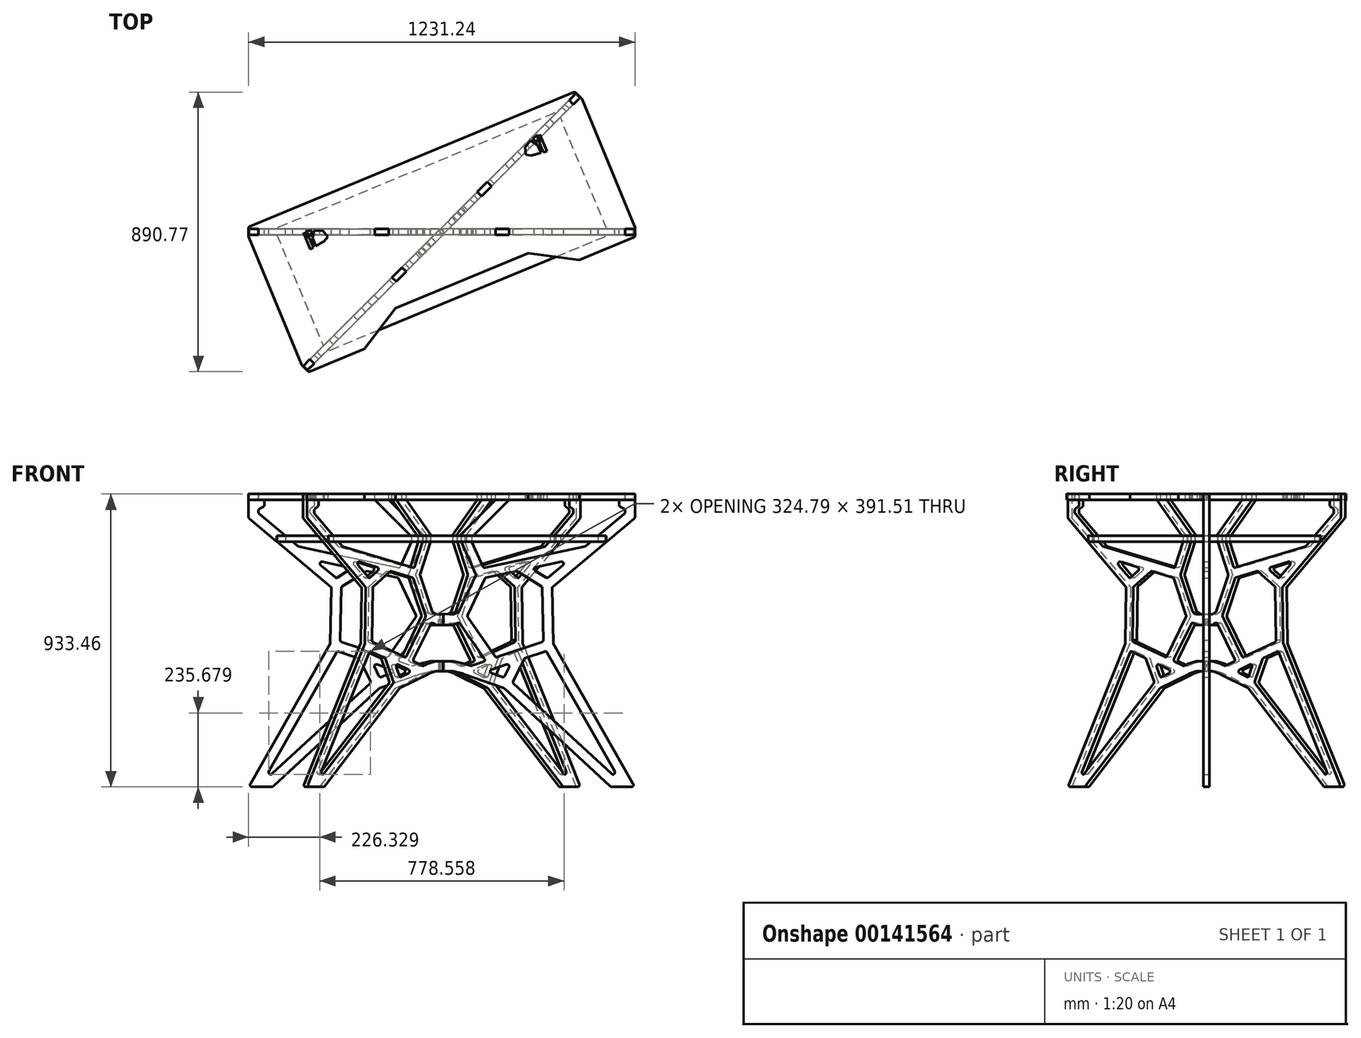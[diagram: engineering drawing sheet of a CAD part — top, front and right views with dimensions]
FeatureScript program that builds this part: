
annotation { "Feature Type Name" : "Feature", "Feature Type Description" : "" }
export const myFeature = defineFeature(function(context is Context, id is Id, definition is map)
    precondition{}
    {
        {
            var Q0;
            Q0=qCreatedBy(makeId("Front.planeOp"),FACE);
            var sketch = newSketch(context, id + "F0", { "sketchPlane" : qUnion([Q0])});
            skLineSegment(sketch, "E0.bottom", {"start": v(-726.46, -550.82) * mm, "end": v(-663.66, -550.82) * mm});
            skLineSegment(sketch, "E0.top", {"start": v(-737.38, 382.63) * mm, "end": v(-705.63, 382.63) * mm});
            skLineSegment(sketch, "E0.left", {"start": v(-737.38, -93.62) * mm, "end": v(-737.38, 230.23) * mm});
            skLineSegment(sketch, "E1", {"start": v(-705.63, 363.58) * mm, "end": v(-686.58, 363.58) * mm});
            skLineSegment(sketch, "E2.bottom", {"start": v(-737.38, 230.23) * mm, "end": v(493.44, 230.23) * mm, "construction": true});
            skLineSegment(sketch, "E2.top", {"start": v(-737.38, 211.18) * mm, "end": v(493.44, 211.18) * mm, "construction": true});
            skLineSegment(sketch, "E2.left", {"start": v(-737.38, 230.23) * mm, "end": v(-737.38, 211.18) * mm});
            skLineSegment(sketch, "E2.right", {"start": v(493.44, 230.23) * mm, "end": v(493.44, 211.18) * mm});
            skLineSegment(sketch, "E3", {"start": v(-735.1, 304.53) * mm, "end": v(-475.84, 87.44) * mm});
            skLineSegment(sketch, "E4", {"start": v(-473.57, 82.44) * mm, "end": v(-477.15, -92) * mm});
            skLineSegment(sketch, "E5", {"start": v(-477.98, -95.02) * mm, "end": v(-731.98, -541.32) * mm});
            skLineSegment(sketch, "E6", {"start": v(-737.38, -93.62) * mm, "end": v(493.78, -93.62) * mm, "construction": true});
            skLineSegment(sketch, "E7", {"start": v(-726.46, -550.82) * mm, "end": v(-661.18, -550.82) * mm});
            skLineSegment(sketch, "E8", {"start": v(-659.36, -549.13) * mm, "end": v(-321.3, -237.33) * mm});
            skLineSegment(sketch, "E9", {"start": v(-319.11, -236) * mm, "end": v(-190.82, -190.7) * mm});
            skLineSegment(sketch, "E10", {"start": v(-190.2, -190.52) * mm, "end": v(-123.3, -174.31) * mm});
            skLineSegment(sketch, "E11", {"start": v(-182.24, 230.23) * mm, "end": v(-228.58, 128.01) * mm});
            skLineSegment(sketch, "E12", {"start": v(-228.55, 122.7) * mm, "end": v(-175.03, 8.55) * mm});
            skLineSegment(sketch, "E13", {"start": v(-171.72, 5.38) * mm, "end": v(-124.24, -14.36) * mm});
            skLineSegment(sketch, "E14", {"start": v(-553, 193.46) * mm, "end": v(-261.6, 132.05) * mm, "construction": true});
            skLineSegment(sketch, "E15", {"start": v(-473.5, 85.48) * mm, "end": v(-383.92, 141.6) * mm, "construction": true});
            skLineSegment(sketch, "E16", {"start": v(-477.18, -93.62) * mm, "end": v(-239.21, -174.12) * mm, "construction": true});
            skLineSegment(sketch, "E17", {"start": v(-320.34, -236.44) * mm, "end": v(-364, -148.67) * mm, "construction": true});
            skLineSegment(sketch, "E18", {"start": v(-192.54, -20.35) * mm, "end": v(-278.62, -144.03) * mm, "construction": true});
            skLineSegment(sketch, "E19.0", {"start": v(-662.9, -509.21) * mm, "end": v(-350.73, -221.27) * mm});
            skLineSegment(sketch, "E20.0", {"start": v(-457.14, -122.59) * mm, "end": v(-672.73, -501.4) * mm});
            skLineSegment(sketch, "E21.0", {"start": v(-199.25, -160.05) * mm, "end": v(-123.3, -141.64) * mm});
            skLineSegment(sketch, "E21.1", {"start": v(-314.2, -200.6) * mm, "end": v(-280.77, -188.8) * mm});
            skLineSegment(sketch, "E22.0", {"start": v(-172.82, -28.55) * mm, "end": v(-124.24, -48.75) * mm});
            skLineSegment(sketch, "E22.1", {"start": v(-258.92, 112.68) * mm, "end": v(-204.28, -3.86) * mm});
            skLineSegment(sketch, "E23.0", {"start": v(-705.63, 324.22) * mm, "end": v(-705.63, 329.87) * mm});
            skLineSegment(sketch, "E24.0", {"start": v(-703.36, 319.36) * mm, "end": v(-580.12, 216.16) * mm});
            skLineSegment(sketch, "E25.0", {"start": v(-441.8, 83.23) * mm, "end": v(-445.22, -83.58) * mm});
            skLineSegment(sketch, "E26.0", {"start": v(-502.23, 166.54) * mm, "end": v(-421.69, 149.57) * mm});
            skLineSegment(sketch, "E27.0", {"start": v(-577.35, 214.82) * mm, "end": v(-259.88, 147.91) * mm});
            skLineSegment(sketch, "E28.0", {"start": v(-438.82, 88.48) * mm, "end": v(-363.71, 135.53) * mm});
            skLineSegment(sketch, "E29.0", {"start": v(-454.1, 116.37) * mm, "end": v(-419.62, 137.97) * mm});
            skLineSegment(sketch, "E30.0", {"start": v(-440.92, -89.12) * mm, "end": v(-298.8, -137.2) * mm});
            skLineSegment(sketch, "E31.0", {"start": v(-449.58, -119.71) * mm, "end": v(-387.8, -140.61) * mm});
            skLineSegment(sketch, "E32.0", {"start": v(-322, -197.44) * mm, "end": v(-335.83, -169.65) * mm});
            skLineSegment(sketch, "E33.0", {"start": v(-349.34, -213.78) * mm, "end": v(-384.15, -143.8) * mm});
            skLineSegment(sketch, "E34.0", {"start": v(-204.81, -10.18) * mm, "end": v(-291.55, -134.82) * mm});
            skLineSegment(sketch, "E35.0", {"start": v(-180.47, -30.78) * mm, "end": v(-258.14, -142.4) * mm});
            skLineSegment(sketch, "E36.trimOffspring", {"start": v(-507.62, 155.46) * mm, "end": v(-461.55, 116.88) * mm});
            skLineSegment(sketch, "E37.trimOffspring", {"start": v(-359.03, 136.36) * mm, "end": v(-263.36, 116.2) * mm});
            skLineSegment(sketch, "E38.trimOffspring", {"start": v(-254.96, -152.04) * mm, "end": v(-217.05, -164.86) * mm});
            skLineSegment(sketch, "E39.trimOffspring", {"start": v(-328.1, -160.8) * mm, "end": v(-280.85, -176.8) * mm});
            skLineSegment(sketch, "E40", {"start": v(-217.45, 230.23) * mm, "end": v(-182.24, 230.23) * mm});
            skPoint(sketch, "E41.orphan", {"position": v(-121.8, 363.58) * mm});
            skLineSegment(sketch, "E42.trimOffspring", {"start": v(-217.45, 230.23) * mm, "end": v(-252.78, 151.53) * mm});
            skPoint(sketch, "E43.visualSharp", {"position": v(-319.5, -202.47) * mm});
            skArc(sketch, "E43.filletArc", {"start": v(-322, -197.44) * mm, "mid": v(-318.7, -200.5) * mm, "end": v(-314.2, -200.6) * mm});
            skLineSegment(sketch, "E44.trimOffspring", {"start": v(-212.9, -164.83) * mm, "end": v(-199.87, -160.23) * mm});
            skPoint(sketch, "E45.visualSharp", {"position": v(-342.68, -155.88) * mm});
            skArc(sketch, "E45.filletArc", {"start": v(-328.1, -160.8) * mm, "mid": v(-334.93, -162.65) * mm, "end": v(-335.83, -169.65) * mm});
            skPoint(sketch, "E46.visualSharp", {"position": v(-263.45, -182.68) * mm});
            skArc(sketch, "E46.filletArc", {"start": v(-280.77, -188.8) * mm, "mid": v(-276.54, -182.77) * mm, "end": v(-280.85, -176.8) * mm});
            skPoint(sketch, "E47.visualSharp", {"position": v(-347.22, -218.04) * mm});
            skArc(sketch, "E47.filletArc", {"start": v(-350.73, -221.27) * mm, "mid": v(-348.79, -217.75) * mm, "end": v(-349.34, -213.78) * mm});
            skPoint(sketch, "E48.visualSharp", {"position": v(-385.31, -141.45) * mm});
            skArc(sketch, "E48.filletArc", {"start": v(-384.15, -143.8) * mm, "mid": v(-385.65, -141.85) * mm, "end": v(-387.8, -140.61) * mm});
            skPoint(sketch, "E49.visualSharp", {"position": v(-454.54, -118.03) * mm});
            skArc(sketch, "E49.filletArc", {"start": v(-449.58, -119.71) * mm, "mid": v(-453.88, -119.8) * mm, "end": v(-457.14, -122.59) * mm});
            skPoint(sketch, "E50.visualSharp", {"position": v(-692.94, -536.91) * mm});
            skArc(sketch, "E50.filletArc", {"start": v(-672.73, -501.4) * mm, "mid": v(-671.16, -509.51) * mm, "end": v(-662.9, -509.21) * mm});
            skPoint(sketch, "E51.visualSharp", {"position": v(-445.33, -87.63) * mm});
            skArc(sketch, "E51.filletArc", {"start": v(-445.23, -82.98) * mm, "mid": v(-444.08, -86.76) * mm, "end": v(-440.92, -89.12) * mm});
            skPoint(sketch, "E52.visualSharp", {"position": v(-294.28, -138.74) * mm});
            skArc(sketch, "E52.filletArc", {"start": v(-298.8, -137.2) * mm, "mid": v(-294.78, -137.22) * mm, "end": v(-291.55, -134.82) * mm});
            skPoint(sketch, "E53.visualSharp", {"position": v(-262.97, -149.33) * mm});
            skArc(sketch, "E53.filletArc", {"start": v(-258.14, -142.4) * mm, "mid": v(-258.96, -148) * mm, "end": v(-254.96, -152.04) * mm});
            skPoint(sketch, "E54.visualSharp", {"position": v(-214.97, -165.57) * mm});
            skArc(sketch, "E54.filletArc", {"start": v(-217.05, -164.86) * mm, "mid": v(-214.98, -165.2) * mm, "end": v(-212.9, -164.83) * mm});
            skPoint(sketch, "E55.visualSharp", {"position": v(-199.56, -160.12) * mm});
            skArc(sketch, "E55.filletArc", {"start": v(-199.25, -160.05) * mm, "mid": v(-199.56, -160.13) * mm, "end": v(-199.87, -160.23) * mm});
            skPoint(sketch, "E56.visualSharp", {"position": v(-190.51, -190.6) * mm});
            skArc(sketch, "E56.filletArc", {"start": v(-190.2, -190.52) * mm, "mid": v(-190.51, -190.6) * mm, "end": v(-190.82, -190.7) * mm});
            skPoint(sketch, "E57.visualSharp", {"position": v(-320.34, -236.44) * mm});
            skArc(sketch, "E57.filletArc", {"start": v(-319.11, -236) * mm, "mid": v(-320.27, -236.55) * mm, "end": v(-321.3, -237.33) * mm});
            skPoint(sketch, "E58.visualSharp", {"position": v(-177.54, -26.58) * mm});
            skArc(sketch, "E58.filletArc", {"start": v(-172.82, -28.55) * mm, "mid": v(-177.04, -28.32) * mm, "end": v(-180.47, -30.78) * mm});
            skPoint(sketch, "E59.visualSharp", {"position": v(-173.99, 6.32) * mm});
            skArc(sketch, "E59.filletArc", {"start": v(-175.03, 8.55) * mm, "mid": v(-173.67, 6.65) * mm, "end": v(-171.72, 5.38) * mm});
            skPoint(sketch, "E60.visualSharp", {"position": v(-202.72, -7.18) * mm});
            skArc(sketch, "E60.filletArc", {"start": v(-204.81, -10.18) * mm, "mid": v(-203.7, -7.1) * mm, "end": v(-204.28, -3.86) * mm});
            skPoint(sketch, "E61.visualSharp", {"position": v(-477.18, -93.62) * mm});
            skArc(sketch, "E61.filletArc", {"start": v(-477.98, -95.02) * mm, "mid": v(-477.37, -93.56) * mm, "end": v(-477.15, -92) * mm});
            skPoint(sketch, "E62.visualSharp", {"position": v(-473.5, 85.48) * mm});
            skArc(sketch, "E62.filletArc", {"start": v(-473.57, 82.44) * mm, "mid": v(-474.14, 85.2) * mm, "end": v(-475.84, 87.44) * mm});
            skPoint(sketch, "E63.visualSharp", {"position": v(-441.73, 86.66) * mm});
            skArc(sketch, "E63.filletArc", {"start": v(-438.82, 88.48) * mm, "mid": v(-440.97, 86.23) * mm, "end": v(-441.8, 83.23) * mm});
            skPoint(sketch, "E64.visualSharp", {"position": v(-458.02, 113.92) * mm});
            skArc(sketch, "E64.filletArc", {"start": v(-461.55, 116.88) * mm, "mid": v(-457.91, 115.42) * mm, "end": v(-454.1, 116.37) * mm});
            skPoint(sketch, "E65.visualSharp", {"position": v(-260.26, 115.55) * mm});
            skArc(sketch, "E65.filletArc", {"start": v(-258.92, 112.68) * mm, "mid": v(-260.72, 114.96) * mm, "end": v(-263.36, 116.2) * mm});
            skPoint(sketch, "E66.visualSharp", {"position": v(-361.54, 136.89) * mm});
            skArc(sketch, "E66.filletArc", {"start": v(-359.03, 136.36) * mm, "mid": v(-361.45, 136.4) * mm, "end": v(-363.71, 135.53) * mm});
            skPoint(sketch, "E67.visualSharp", {"position": v(-406.3, 146.32) * mm});
            skArc(sketch, "E67.filletArc", {"start": v(-419.62, 137.97) * mm, "mid": v(-416.74, 144.46) * mm, "end": v(-421.69, 149.57) * mm});
            skPoint(sketch, "E68.visualSharp", {"position": v(-254.88, 146.86) * mm});
            skArc(sketch, "E68.filletArc", {"start": v(-259.88, 147.91) * mm, "mid": v(-255.7, 148.47) * mm, "end": v(-252.78, 151.53) * mm});
            skPoint(sketch, "E69.visualSharp", {"position": v(-229.79, 125.35) * mm});
            skArc(sketch, "E69.filletArc", {"start": v(-228.58, 128.01) * mm, "mid": v(-229.15, 125.35) * mm, "end": v(-228.55, 122.7) * mm});
            skPoint(sketch, "E70.visualSharp", {"position": v(-527.12, 171.78) * mm});
            skArc(sketch, "E70.filletArc", {"start": v(-502.23, 166.54) * mm, "mid": v(-509.25, 163.1) * mm, "end": v(-507.62, 155.46) * mm});
            skPoint(sketch, "E71.visualSharp", {"position": v(-578.9, 215.14) * mm});
            skArc(sketch, "E71.filletArc", {"start": v(-580.12, 216.16) * mm, "mid": v(-578.82, 215.32) * mm, "end": v(-577.35, 214.82) * mm});
            skLineSegment(sketch, "E72", {"start": v(-737.38, 382.63) * mm, "end": v(-737.38, 309.4) * mm});
            skPoint(sketch, "E73.visualSharp", {"position": v(-737.38, 306.43) * mm});
            skArc(sketch, "E73.filletArc", {"start": v(-737.38, 309.4) * mm, "mid": v(-736.78, 306.71) * mm, "end": v(-735.1, 304.53) * mm});
            skPoint(sketch, "E74.visualSharp", {"position": v(-705.63, 321.26) * mm});
            skArc(sketch, "E74.filletArc", {"start": v(-705.63, 324.22) * mm, "mid": v(-705.03, 321.54) * mm, "end": v(-703.36, 319.36) * mm});
            skArc(sketch, "E75.MirrorCS", {"start": v(234.38, -95.02) * mm, "mid": v(233.78, -93.56) * mm, "end": v(233.55, -92) * mm});
            skArc(sketch, "E76.MirrorCS", {"start": v(195.22, 88.48) * mm, "mid": v(197.38, 86.23) * mm, "end": v(198.2, 83.23) * mm});
            skArc(sketch, "E77.MirrorCS", {"start": v(-26.54, -164.86) * mm, "mid": v(-28.62, -165.2) * mm, "end": v(-30.7, -164.83) * mm});
            skArc(sketch, "E78.MirrorCS", {"start": v(-44.35, -160.05) * mm, "mid": v(-44.04, -160.13) * mm, "end": v(-43.73, -160.23) * mm});
            skLineSegment(sketch, "E79.MirrorCS", {"start": v(-30.7, -164.83) * mm, "end": v(-43.73, -160.23) * mm});
            skArc(sketch, "E80.MirrorCS", {"start": v(229.97, 82.44) * mm, "mid": v(230.54, 85.2) * mm, "end": v(232.25, 87.44) * mm});
            skArc(sketch, "E81.MirrorCS", {"start": v(75.51, -236) * mm, "mid": v(76.68, -236.55) * mm, "end": v(77.7, -237.33) * mm});
            skLineSegment(sketch, "E82.MirrorCS", {"start": v(78.41, -197.44) * mm, "end": v(92.23, -169.65) * mm});
            skArc(sketch, "E83.MirrorCS", {"start": v(-70.78, -28.55) * mm, "mid": v(-66.56, -28.32) * mm, "end": v(-63.13, -30.78) * mm});
            skArc(sketch, "E84.MirrorCS", {"start": v(-53.4, -190.52) * mm, "mid": v(-53.08, -190.6) * mm, "end": v(-52.78, -190.7) * mm});
            skArc(sketch, "E85.MirrorCS", {"start": v(115.43, 136.36) * mm, "mid": v(117.86, 136.4) * mm, "end": v(120.11, 135.53) * mm});
            skArc(sketch, "E86.MirrorCS", {"start": v(78.41, -197.44) * mm, "mid": v(75.1, -200.5) * mm, "end": v(70.61, -200.6) * mm});
            skArc(sketch, "E87.MirrorCS", {"start": v(84.51, -160.8) * mm, "mid": v(91.33, -162.65) * mm, "end": v(92.23, -169.65) * mm});
            skArc(sketch, "E88.MirrorCS", {"start": v(336.52, 216.16) * mm, "mid": v(335.22, 215.32) * mm, "end": v(333.75, 214.82) * mm});
            skArc(sketch, "E89.MirrorCS", {"start": v(15.32, 112.68) * mm, "mid": v(17.13, 114.96) * mm, "end": v(19.76, 116.2) * mm});
            skArc(sketch, "E90.MirrorCS", {"start": v(462.03, 324.22) * mm, "mid": v(461.44, 321.54) * mm, "end": v(459.76, 319.36) * mm});
            skArc(sketch, "E91.MirrorCS", {"start": v(217.96, 116.88) * mm, "mid": v(214.32, 115.42) * mm, "end": v(210.5, 116.37) * mm});
            skArc(sketch, "E92.MirrorCS", {"start": v(140.55, -143.8) * mm, "mid": v(142.06, -141.85) * mm, "end": v(144.2, -140.61) * mm});
            skArc(sketch, "E93.MirrorCS", {"start": v(16.29, 147.91) * mm, "mid": v(12.1, 148.47) * mm, "end": v(9.19, 151.53) * mm});
            skArc(sketch, "E94.MirrorCS", {"start": v(-68.57, 8.55) * mm, "mid": v(-69.93, 6.65) * mm, "end": v(-71.88, 5.38) * mm});
            skArc(sketch, "E95.MirrorCS", {"start": v(107.13, -221.27) * mm, "mid": v(105.19, -217.75) * mm, "end": v(105.75, -213.78) * mm});
            skArc(sketch, "E96.MirrorCS", {"start": v(55.2, -137.2) * mm, "mid": v(51.18, -137.22) * mm, "end": v(47.95, -134.82) * mm});
            skLineSegment(sketch, "E97.MirrorCS", {"start": v(210.5, 116.37) * mm, "end": v(176.03, 137.97) * mm});
            skLineSegment(sketch, "E98.MirrorCS", {"start": v(76.75, -236.44) * mm, "end": v(120.4, -148.67) * mm, "construction": true});
            skArc(sketch, "E99.MirrorCS", {"start": v(-15.02, 128.01) * mm, "mid": v(-14.45, 125.35) * mm, "end": v(-15.05, 122.7) * mm});
            skArc(sketch, "E100.MirrorCS", {"start": v(176.03, 137.97) * mm, "mid": v(173.15, 144.46) * mm, "end": v(178.09, 149.57) * mm});
            skArc(sketch, "E101.MirrorCS", {"start": v(201.64, -82.98) * mm, "mid": v(200.49, -86.76) * mm, "end": v(197.32, -89.12) * mm});
            skArc(sketch, "E102.MirrorCS", {"start": v(205.99, -119.71) * mm, "mid": v(210.28, -119.8) * mm, "end": v(213.54, -122.59) * mm});
            skArc(sketch, "E103.MirrorCS", {"start": v(493.78, 309.4) * mm, "mid": v(493.19, 306.71) * mm, "end": v(491.5, 304.53) * mm});
            skArc(sketch, "E104.MirrorCS", {"start": v(258.64, 166.54) * mm, "mid": v(265.66, 163.1) * mm, "end": v(264.02, 155.46) * mm});
            skLineSegment(sketch, "E105.MirrorCS", {"start": v(11.37, -152.04) * mm, "end": v(-26.54, -164.86) * mm});
            skLineSegment(sketch, "E106.MirrorCS", {"start": v(493.78, -550.82) * mm, "end": v(417.58, -550.82) * mm});
            skLineSegment(sketch, "E107.MirrorCS", {"start": v(70.61, -200.6) * mm, "end": v(37.18, -188.8) * mm});
            skLineSegment(sketch, "E108.MirrorCS", {"start": v(493.78, 230.23) * mm, "end": v(493.78, 211.18) * mm});
            skArc(sketch, "E109.MirrorCS", {"start": v(429.13, -501.4) * mm, "mid": v(427.56, -509.51) * mm, "end": v(419.3, -509.21) * mm});
            skLineSegment(sketch, "E110.MirrorCS", {"start": v(84.51, -160.8) * mm, "end": v(37.26, -176.8) * mm});
            skArc(sketch, "E111.MirrorCS", {"start": v(37.18, -188.8) * mm, "mid": v(32.94, -182.77) * mm, "end": v(37.26, -176.8) * mm});
            skArc(sketch, "E112.MirrorCS", {"start": v(14.54, -142.4) * mm, "mid": v(15.36, -148) * mm, "end": v(11.37, -152.04) * mm});
            skArc(sketch, "E113.MirrorCS", {"start": v(-38.78, -10.18) * mm, "mid": v(-39.9, -7.1) * mm, "end": v(-39.32, -3.86) * mm});
            skLineSegment(sketch, "E114.MirrorCS", {"start": v(229.91, 85.48) * mm, "end": v(140.32, 141.6) * mm, "construction": true});
            skLineSegment(sketch, "E115.MirrorCS", {"start": v(105.75, -213.78) * mm, "end": v(140.55, -143.8) * mm});
            skLineSegment(sketch, "E116.MirrorCS", {"start": v(-26.15, 230.23) * mm, "end": v(-61.35, 230.23) * mm});
            skLineSegment(sketch, "E117.MirrorCS", {"start": v(264.02, 155.46) * mm, "end": v(217.96, 116.88) * mm});
            skLineSegment(sketch, "E118.MirrorCS", {"start": v(462.03, 324.22) * mm, "end": v(462.03, 329.87) * mm});
            skLineSegment(sketch, "E119.MirrorCS", {"start": v(-737.04, 230.23) * mm, "end": v(-737.04, 211.18) * mm});
            skLineSegment(sketch, "E120.MirrorCS", {"start": v(482.86, -550.82) * mm, "end": v(420.06, -550.82) * mm});
            skLineSegment(sketch, "E121.MirrorCS", {"start": v(-71.88, 5.38) * mm, "end": v(-119.36, -14.36) * mm});
            skPoint(sketch, "E122.MirrorP", {"position": v(-28.62, -165.57) * mm});
            skLineSegment(sketch, "E123.MirrorCS", {"start": v(-38.78, -10.18) * mm, "end": v(47.95, -134.82) * mm});
            skLineSegment(sketch, "E124.MirrorCS", {"start": v(-51.05, -20.35) * mm, "end": v(35.03, -144.03) * mm, "construction": true});
            skLineSegment(sketch, "E125.MirrorCS", {"start": v(309.41, 193.46) * mm, "end": v(18.01, 132.05) * mm, "construction": true});
            skLineSegment(sketch, "E126.MirrorCS", {"start": v(233.58, -93.62) * mm, "end": v(-4.38, -174.12) * mm, "construction": true});
            skLineSegment(sketch, "E127.MirrorCS", {"start": v(258.64, 166.54) * mm, "end": v(178.09, 149.57) * mm});
            skPoint(sketch, "E128.MirrorP", {"position": v(99.08, -155.88) * mm});
            skLineSegment(sketch, "E129.MirrorCS", {"start": v(-70.78, -28.55) * mm, "end": v(-119.36, -48.75) * mm});
            skPoint(sketch, "E130.MirrorP", {"position": v(-66.05, -26.58) * mm});
            skPoint(sketch, "E131.MirrorP", {"position": v(162.7, 146.32) * mm});
            skPoint(sketch, "E132.MirrorP", {"position": v(198.13, 86.66) * mm});
            skLineSegment(sketch, "E133.MirrorCS", {"start": v(-63.13, -30.78) * mm, "end": v(14.54, -142.4) * mm});
            skLineSegment(sketch, "E134.MirrorCS", {"start": v(205.99, -119.71) * mm, "end": v(144.2, -140.61) * mm});
            skLineSegment(sketch, "E135.MirrorCS", {"start": v(195.22, 88.48) * mm, "end": v(120.11, 135.53) * mm});
            skPoint(sketch, "E136.MirrorP", {"position": v(50.68, -138.74) * mm});
            skLineSegment(sketch, "E137.MirrorCS", {"start": v(-44.35, -160.05) * mm, "end": v(-120.3, -141.64) * mm});
            skLineSegment(sketch, "E138.MirrorCS", {"start": v(-53.4, -190.52) * mm, "end": v(-120.3, -174.31) * mm});
            skLineSegment(sketch, "E139.MirrorCS", {"start": v(197.32, -89.12) * mm, "end": v(55.2, -137.2) * mm});
            skPoint(sketch, "E140.MirrorP", {"position": v(462.03, 321.26) * mm});
            skPoint(sketch, "E141.MirrorP", {"position": v(16.66, 115.55) * mm});
            skPoint(sketch, "E142.MirrorP", {"position": v(-40.87, -7.18) * mm});
            skPoint(sketch, "E143.MirrorP", {"position": v(11.28, 146.86) * mm});
            skLineSegment(sketch, "E144.MirrorCS", {"start": v(-26.15, 230.23) * mm, "end": v(9.19, 151.53) * mm});
            skLineSegment(sketch, "E145.MirrorCS", {"start": v(419.3, -509.21) * mm, "end": v(107.13, -221.27) * mm});
            skLineSegment(sketch, "E146.MirrorCS", {"start": v(-15.05, 122.7) * mm, "end": v(-68.57, 8.55) * mm});
            skLineSegment(sketch, "E147.MirrorCS", {"start": v(198.2, 83.23) * mm, "end": v(201.62, -83.58) * mm});
            skLineSegment(sketch, "E148.MirrorCS", {"start": v(459.76, 319.36) * mm, "end": v(336.52, 216.16) * mm});
            skLineSegment(sketch, "E149.MirrorCS", {"start": v(493.78, 382.63) * mm, "end": v(493.78, 309.4) * mm});
            skPoint(sketch, "E150.MirrorP", {"position": v(19.86, -182.68) * mm});
            skPoint(sketch, "E151.MirrorP", {"position": v(214.42, 113.92) * mm});
            skLineSegment(sketch, "E152.MirrorCS", {"start": v(-61.35, 230.23) * mm, "end": v(-15.02, 128.01) * mm});
            skPoint(sketch, "E153.MirrorP", {"position": v(283.52, 171.78) * mm});
            skPoint(sketch, "E154.MirrorP", {"position": v(141.72, -141.45) * mm});
            skPoint(sketch, "E155.MirrorP", {"position": v(493.78, 306.43) * mm});
            skPoint(sketch, "E156.MirrorP", {"position": v(229.91, 85.48) * mm});
            skLineSegment(sketch, "E157.MirrorCS", {"start": v(213.54, -122.59) * mm, "end": v(429.13, -501.4) * mm});
            skLineSegment(sketch, "E158.MirrorCS", {"start": v(493.78, -93.62) * mm, "end": v(493.78, 230.23) * mm});
            skPoint(sketch, "E159.MirrorP", {"position": v(19.37, -149.33) * mm});
            skLineSegment(sketch, "E160.MirrorCS", {"start": v(333.75, 214.82) * mm, "end": v(16.29, 147.91) * mm});
            skPoint(sketch, "E161.MirrorP", {"position": v(335.3, 215.14) * mm});
            skLineSegment(sketch, "E162.MirrorCS", {"start": v(491.5, 304.53) * mm, "end": v(232.25, 87.44) * mm});
            skPoint(sketch, "E163.MirrorP", {"position": v(75.9, -202.47) * mm});
            skPoint(sketch, "E164.MirrorP", {"position": v(-53.08, -190.6) * mm});
            skLineSegment(sketch, "E165.MirrorCS", {"start": v(75.51, -236) * mm, "end": v(-52.78, -190.7) * mm});
            skPoint(sketch, "E166.MirrorP", {"position": v(117.94, 136.89) * mm});
            skPoint(sketch, "E167.MirrorP", {"position": v(-13.8, 125.35) * mm});
            skLineSegment(sketch, "E168.MirrorCS", {"start": v(415.76, -549.13) * mm, "end": v(77.7, -237.33) * mm});
            skLineSegment(sketch, "E169.MirrorCS", {"start": v(234.38, -95.02) * mm, "end": v(488.38, -541.32) * mm});
            skPoint(sketch, "E170.MirrorP", {"position": v(210.95, -118.03) * mm});
            skLineSegment(sketch, "E171.MirrorCS", {"start": v(15.32, 112.68) * mm, "end": v(-39.32, -3.86) * mm});
            skPoint(sketch, "E172.MirrorP", {"position": v(-69.61, 6.32) * mm});
            skPoint(sketch, "E173.MirrorP", {"position": v(-44.04, -160.12) * mm});
            skPoint(sketch, "E174.MirrorP", {"position": v(76.75, -236.44) * mm});
            skPoint(sketch, "E175.MirrorP", {"position": v(103.63, -218.04) * mm});
            skPoint(sketch, "E176.MirrorP", {"position": v(201.73, -87.63) * mm});
            skLineSegment(sketch, "E177.MirrorCS", {"start": v(229.97, 82.44) * mm, "end": v(233.55, -92) * mm});
            skLineSegment(sketch, "E178.MirrorCS", {"start": v(115.43, 136.36) * mm, "end": v(19.76, 116.2) * mm});
            skPoint(sketch, "E179.MirrorP", {"position": v(233.58, -93.62) * mm});
            skLineSegment(sketch, "E180", {"start": v(-686.58, 363.58) * mm, "end": v(-686.58, 348.2) * mm});
            skLineSegment(sketch, "E181", {"start": v(-689.75, 342.7) * mm, "end": v(-702.45, 335.37) * mm});
            skLineSegment(sketch, "E182.trimOffspring", {"start": v(-705.63, 363.58) * mm, "end": v(-705.63, 382.63) * mm});
            skPoint(sketch, "E183.visualSharp", {"position": v(-705.63, 333.54) * mm});
            skArc(sketch, "E183.filletArc", {"start": v(-702.45, 335.37) * mm, "mid": v(-704.78, 333.04) * mm, "end": v(-705.63, 329.87) * mm});
            skPoint(sketch, "E184.visualSharp", {"position": v(-686.58, 344.53) * mm});
            skArc(sketch, "E184.filletArc", {"start": v(-689.75, 342.7) * mm, "mid": v(-687.43, 345.03) * mm, "end": v(-686.58, 348.2) * mm});
            skLineSegment(sketch, "E185.trimOffspring", {"start": v(462.03, 382.63) * mm, "end": v(493.78, 382.63) * mm});
            skLineSegment(sketch, "E186", {"start": v(-182.24, 230.23) * mm, "end": v(-182.24, 249.28) * mm});
            skLineSegment(sketch, "E187", {"start": v(-182.24, 249.28) * mm, "end": v(-217.45, 249.28) * mm});
            skLineSegment(sketch, "E188", {"start": v(-217.45, 249.28) * mm, "end": v(-217.45, 230.23) * mm});
            skLineSegment(sketch, "E189", {"start": v(-61.35, 230.23) * mm, "end": v(-61.35, 249.28) * mm});
            skLineSegment(sketch, "E190", {"start": v(-61.35, 249.28) * mm, "end": v(-26.15, 249.28) * mm});
            skLineSegment(sketch, "E191", {"start": v(-26.15, 249.28) * mm, "end": v(-26.15, 230.23) * mm});
            skLineSegment(sketch, "E192", {"start": v(462.03, 363.58) * mm, "end": v(442.98, 363.58) * mm});
            skLineSegment(sketch, "E193", {"start": v(442.98, 363.58) * mm, "end": v(442.98, 348.2) * mm});
            skLineSegment(sketch, "E194", {"start": v(446.16, 342.7) * mm, "end": v(458.86, 335.37) * mm});
            skLineSegment(sketch, "E195.trimOffspring", {"start": v(462.03, 363.58) * mm, "end": v(462.03, 382.63) * mm});
            skPoint(sketch, "E196.visualSharp", {"position": v(442.98, 344.53) * mm});
            skArc(sketch, "E196.filletArc", {"start": v(442.98, 348.2) * mm, "mid": v(443.83, 345.03) * mm, "end": v(446.16, 342.7) * mm});
            skPoint(sketch, "E197.visualSharp", {"position": v(462.03, 333.54) * mm});
            skArc(sketch, "E197.filletArc", {"start": v(462.03, 329.87) * mm, "mid": v(461.18, 333.04) * mm, "end": v(458.86, 335.37) * mm});
            skPoint(sketch, "E198.visualSharp", {"position": v(417.58, -550.82) * mm});
            skArc(sketch, "E198.filletArc", {"start": v(415.76, -549.13) * mm, "mid": v(417.75, -550.38) * mm, "end": v(420.06, -550.82) * mm});
            skPoint(sketch, "E199.visualSharp", {"position": v(493.78, -550.82) * mm});
            skArc(sketch, "E199.filletArc", {"start": v(482.86, -550.82) * mm, "mid": v(488.35, -547.66) * mm, "end": v(488.38, -541.32) * mm});
            skPoint(sketch, "E200.visualSharp", {"position": v(-737.38, -550.82) * mm});
            skArc(sketch, "E200.filletArc", {"start": v(-731.98, -541.32) * mm, "mid": v(-731.95, -547.66) * mm, "end": v(-726.46, -550.82) * mm});
            skPoint(sketch, "E201.visualSharp", {"position": v(-661.18, -550.82) * mm});
            skArc(sketch, "E201.filletArc", {"start": v(-663.66, -550.82) * mm, "mid": v(-661.35, -550.38) * mm, "end": v(-659.36, -549.13) * mm});
            skPoint(sketch, "E202.visualSharp", {"position": v(-121.8, -173.95) * mm});
            skArc(sketch, "E202.filletArc", {"start": v(-120.3, -174.31) * mm, "mid": v(-121.8, -174.13) * mm, "end": v(-123.3, -174.31) * mm});
            skPoint(sketch, "E203.visualSharp", {"position": v(-121.8, -141.28) * mm});
            skArc(sketch, "E203.filletArc", {"start": v(-120.3, -141.64) * mm, "mid": v(-121.8, -141.47) * mm, "end": v(-123.3, -141.64) * mm});
            skPoint(sketch, "E204.visualSharp", {"position": v(-121.8, -49.76) * mm});
            skArc(sketch, "E204.filletArc", {"start": v(-124.24, -48.75) * mm, "mid": v(-121.8, -49.23) * mm, "end": v(-119.36, -48.75) * mm});
            skPoint(sketch, "E205.visualSharp", {"position": v(-121.8, -15.38) * mm});
            skArc(sketch, "E205.filletArc", {"start": v(-124.24, -14.36) * mm, "mid": v(-121.8, -14.85) * mm, "end": v(-119.36, -14.36) * mm});
            skLineSegment(sketch, "E206", {"start": v(-121.8, -14.85) * mm, "end": v(-121.8, -49.23) * mm});
            skPoint(sketch, "E207", {"position": v(-121.8, -32.04) * mm});
            skLineSegment(sketch, "E208", {"start": v(-121.8, -32.04) * mm, "end": v(-79.18, -32.04) * mm});
            skLineSegment(sketch, "E209", {"start": v(-121.8, -32.04) * mm, "end": v(-164.42, -32.04) * mm});
            skLineSegment(sketch, "E210", {"start": v(-121.8, -141.47) * mm, "end": v(-121.8, -174.13) * mm});
            skPoint(sketch, "E211", {"position": v(-121.8, -157.8) * mm});
            skLineSegment(sketch, "E212", {"start": v(-121.8, -157.8) * mm, "end": v(-53.62, -157.8) * mm});
            skLineSegment(sketch, "E213", {"start": v(-121.8, -157.8) * mm, "end": v(-189.97, -157.8) * mm});
            skSolve(sketch);
        }
        {
            var Q0;
            Q0=qCreatedBy(makeId("Top.planeOp"),FACE);
            cPlane(context, id + "F1", {"entities" : qUnion([Q0]), "cplaneType" : CPlaneType.OFFSET, "offset" : 230.23 * mm, "width" : 152.4 * mm, "height" : 152.4 * mm});
        }
        {
            var Q0;
            Q0=qCreatedBy(id+"F1.planeOp",FACE);
            cPlane(context, id + "F2", {"entities" : qUnion([Q0]), "cplaneType" : CPlaneType.OFFSET, "offset" : 133.35 * mm, "width" : 152.4 * mm, "height" : 152.4 * mm});
        }
        {
            var Q0;
            Q0=sQuery(id+"F0.wireOp",EDGE,"E206");
            cPlane(context, id + "F3", {"entities" : qUnion([Q0]), "cplaneType" : CPlaneType.LINE_ANGLE, "offset" : 25.4 * mm, "angle" : 45 * degree, "width" : 152.4 * mm, "height" : 152.4 * mm});
        }
        {
            var Q0;
            Q0=qCreatedBy(id+"F3.planeOp",FACE);
            var sketch = newSketch(context, id + "F4", { "sketchPlane" : qUnion([Q0])});
            skLineSegment(sketch, "E214.bottom", {"start": v(-518.53, -550.77) * mm, "end": v(-455.73, -550.77) * mm});
            skLineSegment(sketch, "E214.top", {"start": v(-529.45, 382.68) * mm, "end": v(-497.7, 382.68) * mm});
            skLineSegment(sketch, "E215", {"start": v(-497.7, 363.63) * mm, "end": v(-478.65, 363.63) * mm});
            skLineSegment(sketch, "E216", {"start": v(-527.18, 304.58) * mm, "end": v(-267.92, 87.48) * mm});
            skLineSegment(sketch, "E217", {"start": v(-265.64, 82.49) * mm, "end": v(-269.22, -91.96) * mm});
            skLineSegment(sketch, "E218", {"start": v(-270.05, -94.97) * mm, "end": v(-524.05, -541.28) * mm});
            skLineSegment(sketch, "E219", {"start": v(-518.53, -550.77) * mm, "end": v(-453.25, -550.77) * mm});
            skLineSegment(sketch, "E220", {"start": v(-451.43, -549.09) * mm, "end": v(-113.38, -237.28) * mm});
            skLineSegment(sketch, "E221", {"start": v(-111.18, -235.96) * mm, "end": v(17.1, -190.66) * mm});
            skLineSegment(sketch, "E222", {"start": v(17.73, -190.48) * mm, "end": v(49.67, -182.74) * mm});
            skLineSegment(sketch, "E223", {"start": v(25.68, 230.28) * mm, "end": v(-20.65, 128.06) * mm});
            skLineSegment(sketch, "E224", {"start": v(-20.62, 122.74) * mm, "end": v(32.9, 8.6) * mm});
            skLineSegment(sketch, "E225", {"start": v(36.21, 5.43) * mm, "end": v(49.67, -0.17) * mm});
            skLineSegment(sketch, "E226.0", {"start": v(-454.97, -509.17) * mm, "end": v(-142.8, -221.23) * mm});
            skLineSegment(sketch, "E227.0", {"start": v(-249.2, -122.54) * mm, "end": v(-464.8, -501.36) * mm});
            skLineSegment(sketch, "E228.0", {"start": v(8.68, -160) * mm, "end": v(49.67, -150.07) * mm});
            skLineSegment(sketch, "E228.1", {"start": v(-106.28, -200.56) * mm, "end": v(-72.85, -188.75) * mm});
            skLineSegment(sketch, "E229.1", {"start": v(-50.99, 112.73) * mm, "end": v(3.65, -3.82) * mm});
            skLineSegment(sketch, "E230.0", {"start": v(-497.7, 324.27) * mm, "end": v(-497.7, 329.92) * mm});
            skLineSegment(sketch, "E231.0", {"start": v(-495.43, 319.4) * mm, "end": v(-411.75, 249.33) * mm});
            skLineSegment(sketch, "E232.0", {"start": v(-233.87, 83.27) * mm, "end": v(-237.3, -83.53) * mm});
            skLineSegment(sketch, "E233.0", {"start": v(-294.3, 166.59) * mm, "end": v(-213.76, 149.61) * mm});
            skLineSegment(sketch, "E234.0", {"start": v(-369.42, 214.86) * mm, "end": v(-51.96, 147.96) * mm});
            skLineSegment(sketch, "E235.0", {"start": v(-230.9, 88.53) * mm, "end": v(-155.78, 135.57) * mm});
            skLineSegment(sketch, "E236.0", {"start": v(-246.18, 116.42) * mm, "end": v(-211.7, 138.02) * mm});
            skLineSegment(sketch, "E237.0", {"start": v(-233, -89.08) * mm, "end": v(-90.87, -137.16) * mm});
            skLineSegment(sketch, "E238.0", {"start": v(-241.65, -119.67) * mm, "end": v(-179.87, -140.57) * mm});
            skLineSegment(sketch, "E239.0", {"start": v(-114.08, -197.4) * mm, "end": v(-127.9, -169.6) * mm});
            skLineSegment(sketch, "E240.0", {"start": v(-141.42, -213.73) * mm, "end": v(-176.22, -143.76) * mm});
            skLineSegment(sketch, "E241.0", {"start": v(3.11, -10.14) * mm, "end": v(-83.62, -134.77) * mm});
            skLineSegment(sketch, "E242.0", {"start": v(27.46, -30.74) * mm, "end": v(-50.21, -142.35) * mm});
            skLineSegment(sketch, "E243.trimOffspring", {"start": v(-299.7, 155.5) * mm, "end": v(-253.63, 116.93) * mm});
            skLineSegment(sketch, "E244.trimOffspring", {"start": v(-151.1, 136.4) * mm, "end": v(-55.43, 116.24) * mm});
            skLineSegment(sketch, "E245.trimOffspring", {"start": v(-47.04, -152) * mm, "end": v(-9.13, -164.82) * mm});
            skLineSegment(sketch, "E246.trimOffspring", {"start": v(-120.18, -160.76) * mm, "end": v(-72.93, -176.75) * mm});
            skLineSegment(sketch, "E247", {"start": v(8.08, 230.28) * mm, "end": v(25.68, 230.28) * mm});
            skPoint(sketch, "E248.orphan", {"position": v(86.13, 363.63) * mm});
            skLineSegment(sketch, "E249.trimOffspring", {"start": v(-9.52, 230.28) * mm, "end": v(-44.85, 151.57) * mm});
            skPoint(sketch, "E250.visualSharp", {"position": v(-111.58, -202.43) * mm});
            skArc(sketch, "E250.filletArc", {"start": v(-114.08, -197.4) * mm, "mid": v(-110.78, -200.46) * mm, "end": v(-106.28, -200.56) * mm});
            skLineSegment(sketch, "E251.trimOffspring", {"start": v(-4.98, -164.79) * mm, "end": v(8.06, -160.19) * mm});
            skPoint(sketch, "E252.visualSharp", {"position": v(-134.75, -155.83) * mm});
            skArc(sketch, "E252.filletArc", {"start": v(-120.18, -160.76) * mm, "mid": v(-127, -162.6) * mm, "end": v(-127.9, -169.6) * mm});
            skPoint(sketch, "E253.visualSharp", {"position": v(-55.52, -182.64) * mm});
            skArc(sketch, "E253.filletArc", {"start": v(-72.85, -188.75) * mm, "mid": v(-68.61, -182.72) * mm, "end": v(-72.93, -176.75) * mm});
            skPoint(sketch, "E254.visualSharp", {"position": v(-139.3, -218) * mm});
            skArc(sketch, "E254.filletArc", {"start": v(-142.8, -221.23) * mm, "mid": v(-140.86, -217.7) * mm, "end": v(-141.42, -213.73) * mm});
            skPoint(sketch, "E255.visualSharp", {"position": v(-177.39, -141.4) * mm});
            skArc(sketch, "E255.filletArc", {"start": v(-176.22, -143.76) * mm, "mid": v(-177.73, -141.8) * mm, "end": v(-179.87, -140.57) * mm});
            skPoint(sketch, "E256.visualSharp", {"position": v(-246.62, -117.99) * mm});
            skArc(sketch, "E256.filletArc", {"start": v(-241.65, -119.67) * mm, "mid": v(-245.95, -119.75) * mm, "end": v(-249.2, -122.54) * mm});
            skPoint(sketch, "E257.visualSharp", {"position": v(-485, -536.87) * mm});
            skArc(sketch, "E257.filletArc", {"start": v(-464.8, -501.36) * mm, "mid": v(-463.23, -509.47) * mm, "end": v(-454.97, -509.17) * mm});
            skPoint(sketch, "E258.visualSharp", {"position": v(-237.4, -87.59) * mm});
            skArc(sketch, "E258.filletArc", {"start": v(-237.3, -82.93) * mm, "mid": v(-236.16, -86.71) * mm, "end": v(-233, -89.08) * mm});
            skPoint(sketch, "E259.visualSharp", {"position": v(-86.35, -138.7) * mm});
            skArc(sketch, "E259.filletArc", {"start": v(-90.87, -137.16) * mm, "mid": v(-86.85, -137.18) * mm, "end": v(-83.62, -134.77) * mm});
            skPoint(sketch, "E260.visualSharp", {"position": v(-55.04, -149.28) * mm});
            skArc(sketch, "E260.filletArc", {"start": v(-50.21, -142.35) * mm, "mid": v(-51.03, -147.96) * mm, "end": v(-47.04, -152) * mm});
            skPoint(sketch, "E261.visualSharp", {"position": v(-7.05, -165.52) * mm});
            skArc(sketch, "E261.filletArc", {"start": v(-9.13, -164.82) * mm, "mid": v(-7.05, -165.15) * mm, "end": v(-4.98, -164.79) * mm});
            skPoint(sketch, "E262.visualSharp", {"position": v(8.37, -160.08) * mm});
            skArc(sketch, "E262.filletArc", {"start": v(8.68, -160) * mm, "mid": v(8.37, -160.09) * mm, "end": v(8.06, -160.19) * mm});
            skPoint(sketch, "E263.visualSharp", {"position": v(17.41, -190.55) * mm});
            skArc(sketch, "E263.filletArc", {"start": v(17.73, -190.48) * mm, "mid": v(17.42, -190.56) * mm, "end": v(17.1, -190.66) * mm});
            skPoint(sketch, "E264.visualSharp", {"position": v(-112.42, -236.4) * mm});
            skArc(sketch, "E264.filletArc", {"start": v(-111.18, -235.96) * mm, "mid": v(-112.35, -236.5) * mm, "end": v(-113.38, -237.28) * mm});
            skPoint(sketch, "E265.visualSharp", {"position": v(30.38, -26.54) * mm});
            skArc(sketch, "E265.filletArc", {"start": v(35.1, -28.5) * mm, "mid": v(30.89, -28.27) * mm, "end": v(27.46, -30.74) * mm});
            skPoint(sketch, "E266.visualSharp", {"position": v(33.94, 6.37) * mm});
            skArc(sketch, "E266.filletArc", {"start": v(32.9, 8.6) * mm, "mid": v(34.26, 6.7) * mm, "end": v(36.21, 5.43) * mm});
            skPoint(sketch, "E267.visualSharp", {"position": v(5.2, -7.13) * mm});
            skArc(sketch, "E267.filletArc", {"start": v(3.11, -10.14) * mm, "mid": v(4.23, -7.05) * mm, "end": v(3.65, -3.82) * mm});
            skPoint(sketch, "E268.visualSharp", {"position": v(-269.25, -93.57) * mm});
            skArc(sketch, "E268.filletArc", {"start": v(-270.05, -94.97) * mm, "mid": v(-269.45, -93.52) * mm, "end": v(-269.22, -91.96) * mm});
            skPoint(sketch, "E269.visualSharp", {"position": v(-265.58, 85.53) * mm});
            skArc(sketch, "E269.filletArc", {"start": v(-265.64, 82.49) * mm, "mid": v(-266.21, 85.24) * mm, "end": v(-267.92, 87.48) * mm});
            skPoint(sketch, "E270.visualSharp", {"position": v(-233.8, 86.7) * mm});
            skArc(sketch, "E270.filletArc", {"start": v(-230.9, 88.53) * mm, "mid": v(-233.05, 86.28) * mm, "end": v(-233.87, 83.27) * mm});
            skPoint(sketch, "E271.visualSharp", {"position": v(-250.09, 113.97) * mm});
            skArc(sketch, "E271.filletArc", {"start": v(-253.63, 116.93) * mm, "mid": v(-249.98, 115.46) * mm, "end": v(-246.18, 116.42) * mm});
            skPoint(sketch, "E272.visualSharp", {"position": v(-52.33, 115.6) * mm});
            skArc(sketch, "E272.filletArc", {"start": v(-50.99, 112.73) * mm, "mid": v(-52.8, 115) * mm, "end": v(-55.43, 116.24) * mm});
            skPoint(sketch, "E273.visualSharp", {"position": v(-153.61, 136.93) * mm});
            skArc(sketch, "E273.filletArc", {"start": v(-151.1, 136.4) * mm, "mid": v(-153.52, 136.44) * mm, "end": v(-155.78, 135.57) * mm});
            skPoint(sketch, "E274.visualSharp", {"position": v(-198.36, 146.37) * mm});
            skArc(sketch, "E274.filletArc", {"start": v(-211.7, 138.02) * mm, "mid": v(-208.82, 144.5) * mm, "end": v(-213.76, 149.61) * mm});
            skPoint(sketch, "E275.visualSharp", {"position": v(-46.95, 146.9) * mm});
            skArc(sketch, "E275.filletArc", {"start": v(-51.96, 147.96) * mm, "mid": v(-47.77, 148.51) * mm, "end": v(-44.85, 151.57) * mm});
            skPoint(sketch, "E276.visualSharp", {"position": v(-21.86, 125.4) * mm});
            skArc(sketch, "E276.filletArc", {"start": v(-20.65, 128.06) * mm, "mid": v(-21.22, 125.4) * mm, "end": v(-20.62, 122.74) * mm});
            skPoint(sketch, "E277.visualSharp", {"position": v(-319.2, 171.83) * mm});
            skArc(sketch, "E277.filletArc", {"start": v(-294.3, 166.59) * mm, "mid": v(-301.33, 163.15) * mm, "end": v(-299.7, 155.5) * mm});
            skPoint(sketch, "E278.visualSharp", {"position": v(-370.97, 215.2) * mm});
            skArc(sketch, "E278.filletArc", {"start": v(-372.19, 216.2) * mm, "mid": v(-370.89, 215.37) * mm, "end": v(-369.42, 214.86) * mm});
            skLineSegment(sketch, "E279", {"start": v(-529.45, 382.68) * mm, "end": v(-529.45, 309.45) * mm});
            skPoint(sketch, "E280.visualSharp", {"position": v(-529.45, 306.48) * mm});
            skArc(sketch, "E280.filletArc", {"start": v(-529.45, 309.45) * mm, "mid": v(-528.86, 306.76) * mm, "end": v(-527.18, 304.58) * mm});
            skPoint(sketch, "E281.visualSharp", {"position": v(-497.7, 321.3) * mm});
            skArc(sketch, "E281.filletArc", {"start": v(-497.7, 324.27) * mm, "mid": v(-497.1, 321.58) * mm, "end": v(-495.43, 319.4) * mm});
            skArc(sketch, "E282.MirrorCS", {"start": v(442.3, -94.97) * mm, "mid": v(441.7, -93.52) * mm, "end": v(441.48, -91.96) * mm});
            skArc(sketch, "E283.MirrorCS", {"start": v(403.15, 88.53) * mm, "mid": v(405.3, 86.28) * mm, "end": v(406.13, 83.27) * mm});
            skArc(sketch, "E284.MirrorCS", {"start": v(181.38, -164.82) * mm, "mid": v(179.3, -165.15) * mm, "end": v(177.24, -164.79) * mm});
            skArc(sketch, "E285.MirrorCS", {"start": v(163.58, -160) * mm, "mid": v(163.89, -160.09) * mm, "end": v(164.2, -160.19) * mm});
            skLineSegment(sketch, "E286.MirrorCS", {"start": v(177.24, -164.79) * mm, "end": v(164.2, -160.19) * mm});
            skArc(sketch, "E287.MirrorCS", {"start": v(437.9, 82.49) * mm, "mid": v(438.47, 85.24) * mm, "end": v(440.17, 87.48) * mm});
            skArc(sketch, "E288.MirrorCS", {"start": v(283.44, -235.96) * mm, "mid": v(284.6, -236.5) * mm, "end": v(285.63, -237.28) * mm});
            skLineSegment(sketch, "E289.MirrorCS", {"start": v(286.34, -197.4) * mm, "end": v(300.16, -169.6) * mm});
            skArc(sketch, "E290.MirrorCS", {"start": v(137.15, -28.5) * mm, "mid": v(141.37, -28.27) * mm, "end": v(144.8, -30.74) * mm});
            skArc(sketch, "E291.MirrorCS", {"start": v(154.53, -190.48) * mm, "mid": v(154.84, -190.56) * mm, "end": v(155.15, -190.66) * mm});
            skArc(sketch, "E292.MirrorCS", {"start": v(323.36, 136.4) * mm, "mid": v(325.78, 136.44) * mm, "end": v(328.04, 135.57) * mm});
            skArc(sketch, "E293.MirrorCS", {"start": v(286.34, -197.4) * mm, "mid": v(283.04, -200.46) * mm, "end": v(278.54, -200.56) * mm});
            skArc(sketch, "E294.MirrorCS", {"start": v(292.44, -160.76) * mm, "mid": v(299.26, -162.6) * mm, "end": v(300.16, -169.6) * mm});
            skArc(sketch, "E295.MirrorCS", {"start": v(544.45, 216.2) * mm, "mid": v(543.15, 215.37) * mm, "end": v(541.68, 214.86) * mm});
            skArc(sketch, "E296.MirrorCS", {"start": v(223.25, 112.73) * mm, "mid": v(225.05, 115) * mm, "end": v(227.69, 116.24) * mm});
            skArc(sketch, "E297.MirrorCS", {"start": v(669.96, 324.27) * mm, "mid": v(669.36, 321.58) * mm, "end": v(667.69, 319.4) * mm});
            skArc(sketch, "E298.MirrorCS", {"start": v(425.88, 116.93) * mm, "mid": v(422.24, 115.46) * mm, "end": v(418.44, 116.42) * mm});
            skArc(sketch, "E299.MirrorCS", {"start": v(348.48, -143.76) * mm, "mid": v(349.99, -141.8) * mm, "end": v(352.13, -140.57) * mm});
            skArc(sketch, "E300.MirrorCS", {"start": v(224.22, 147.96) * mm, "mid": v(220.03, 148.51) * mm, "end": v(217.11, 151.57) * mm});
            skArc(sketch, "E301.MirrorCS", {"start": v(139.35, 8.6) * mm, "mid": v(138, 6.7) * mm, "end": v(136.04, 5.43) * mm});
            skArc(sketch, "E302.MirrorCS", {"start": v(315.06, -221.23) * mm, "mid": v(313.12, -217.7) * mm, "end": v(313.68, -213.73) * mm});
            skArc(sketch, "E303.MirrorCS", {"start": v(263.13, -137.16) * mm, "mid": v(259.1, -137.18) * mm, "end": v(255.88, -134.77) * mm});
            skLineSegment(sketch, "E304.MirrorCS", {"start": v(418.44, 116.42) * mm, "end": v(383.95, 138.02) * mm});
            skArc(sketch, "E305.MirrorCS", {"start": v(192.9, 128.06) * mm, "mid": v(193.47, 125.4) * mm, "end": v(192.87, 122.74) * mm});
            skArc(sketch, "E306.MirrorCS", {"start": v(383.95, 138.02) * mm, "mid": v(381.07, 144.5) * mm, "end": v(386.02, 149.61) * mm});
            skArc(sketch, "E307.MirrorCS", {"start": v(409.56, -82.93) * mm, "mid": v(408.41, -86.71) * mm, "end": v(405.25, -89.08) * mm});
            skArc(sketch, "E308.MirrorCS", {"start": v(413.91, -119.67) * mm, "mid": v(418.2, -119.75) * mm, "end": v(421.47, -122.54) * mm});
            skArc(sketch, "E309.MirrorCS", {"start": v(701.71, 309.45) * mm, "mid": v(701.11, 306.76) * mm, "end": v(699.44, 304.58) * mm});
            skArc(sketch, "E310.MirrorCS", {"start": v(466.56, 166.59) * mm, "mid": v(473.59, 163.15) * mm, "end": v(471.95, 155.5) * mm});
            skLineSegment(sketch, "E311.MirrorCS", {"start": v(219.3, -152) * mm, "end": v(181.38, -164.82) * mm});
            skLineSegment(sketch, "E312.MirrorCS", {"start": v(701.71, -550.77) * mm, "end": v(625.51, -550.77) * mm});
            skLineSegment(sketch, "E313.MirrorCS", {"start": v(278.54, -200.56) * mm, "end": v(245.1, -188.75) * mm});
            skArc(sketch, "E314.MirrorCS", {"start": v(637.06, -501.36) * mm, "mid": v(635.49, -509.47) * mm, "end": v(627.23, -509.17) * mm});
            skLineSegment(sketch, "E315.MirrorCS", {"start": v(292.44, -160.76) * mm, "end": v(245.18, -176.75) * mm});
            skArc(sketch, "E316.MirrorCS", {"start": v(245.1, -188.75) * mm, "mid": v(240.87, -182.72) * mm, "end": v(245.18, -176.75) * mm});
            skArc(sketch, "E317.MirrorCS", {"start": v(222.47, -142.35) * mm, "mid": v(223.3, -147.96) * mm, "end": v(219.3, -152) * mm});
            skArc(sketch, "E318.MirrorCS", {"start": v(169.15, -10.14) * mm, "mid": v(168.03, -7.05) * mm, "end": v(168.6, -3.82) * mm});
            skLineSegment(sketch, "E319.MirrorCS", {"start": v(313.68, -213.73) * mm, "end": v(348.48, -143.76) * mm});
            skLineSegment(sketch, "E320.MirrorCS", {"start": v(164.17, 230.28) * mm, "end": v(146.57, 230.28) * mm});
            skLineSegment(sketch, "E321.MirrorCS", {"start": v(471.95, 155.5) * mm, "end": v(425.88, 116.93) * mm});
            skLineSegment(sketch, "E322.MirrorCS", {"start": v(669.96, 324.27) * mm, "end": v(669.96, 329.92) * mm});
            skLineSegment(sketch, "E323.MirrorCS", {"start": v(690.8, -550.77) * mm, "end": v(628, -550.77) * mm});
            skLineSegment(sketch, "E324.MirrorCS", {"start": v(136.04, 5.43) * mm, "end": v(122.58, -0.17) * mm});
            skPoint(sketch, "E325.MirrorP", {"position": v(179.3, -165.52) * mm});
            skLineSegment(sketch, "E326.MirrorCS", {"start": v(169.15, -10.14) * mm, "end": v(255.88, -134.77) * mm});
            skLineSegment(sketch, "E327.MirrorCS", {"start": v(466.56, 166.59) * mm, "end": v(386.02, 149.61) * mm});
            skPoint(sketch, "E328.MirrorP", {"position": v(307.01, -155.83) * mm});
            skPoint(sketch, "E329.MirrorP", {"position": v(141.88, -26.54) * mm});
            skPoint(sketch, "E330.MirrorP", {"position": v(370.62, 146.37) * mm});
            skPoint(sketch, "E331.MirrorP", {"position": v(406.06, 86.7) * mm});
            skLineSegment(sketch, "E332.MirrorCS", {"start": v(144.8, -30.74) * mm, "end": v(222.47, -142.35) * mm});
            skLineSegment(sketch, "E333.MirrorCS", {"start": v(413.91, -119.67) * mm, "end": v(352.13, -140.57) * mm});
            skLineSegment(sketch, "E334.MirrorCS", {"start": v(403.15, 88.53) * mm, "end": v(328.04, 135.57) * mm});
            skPoint(sketch, "E335.MirrorP", {"position": v(258.6, -138.7) * mm});
            skLineSegment(sketch, "E336.MirrorCS", {"start": v(163.58, -160) * mm, "end": v(122.59, -150.07) * mm});
            skLineSegment(sketch, "E337.MirrorCS", {"start": v(154.53, -190.48) * mm, "end": v(122.59, -182.74) * mm});
            skLineSegment(sketch, "E338.MirrorCS", {"start": v(405.25, -89.08) * mm, "end": v(263.13, -137.16) * mm});
            skPoint(sketch, "E339.MirrorP", {"position": v(669.96, 321.3) * mm});
            skPoint(sketch, "E340.MirrorP", {"position": v(224.6, 115.6) * mm});
            skPoint(sketch, "E341.MirrorP", {"position": v(167.05, -7.13) * mm});
            skPoint(sketch, "E342.MirrorP", {"position": v(219.2, 146.9) * mm});
            skLineSegment(sketch, "E343.MirrorCS", {"start": v(181.78, 230.28) * mm, "end": v(217.11, 151.57) * mm});
            skLineSegment(sketch, "E344.MirrorCS", {"start": v(627.23, -509.17) * mm, "end": v(315.06, -221.23) * mm});
            skLineSegment(sketch, "E345.MirrorCS", {"start": v(192.87, 122.74) * mm, "end": v(139.35, 8.6) * mm});
            skLineSegment(sketch, "E346.MirrorCS", {"start": v(406.13, 83.27) * mm, "end": v(409.55, -83.53) * mm});
            skLineSegment(sketch, "E347.MirrorCS", {"start": v(667.69, 319.4) * mm, "end": v(584, 249.33) * mm});
            skLineSegment(sketch, "E348.MirrorCS", {"start": v(701.71, 382.68) * mm, "end": v(701.71, 309.45) * mm});
            skPoint(sketch, "E349.MirrorP", {"position": v(227.78, -182.64) * mm});
            skPoint(sketch, "E350.MirrorP", {"position": v(422.35, 113.97) * mm});
            skLineSegment(sketch, "E351.MirrorCS", {"start": v(146.57, 230.28) * mm, "end": v(192.9, 128.06) * mm});
            skPoint(sketch, "E352.MirrorP", {"position": v(491.45, 171.83) * mm});
            skPoint(sketch, "E353.MirrorP", {"position": v(349.64, -141.4) * mm});
            skPoint(sketch, "E354.MirrorP", {"position": v(701.71, 306.48) * mm});
            skPoint(sketch, "E355.MirrorP", {"position": v(437.84, 85.53) * mm});
            skLineSegment(sketch, "E356.MirrorCS", {"start": v(421.47, -122.54) * mm, "end": v(637.06, -501.36) * mm});
            skPoint(sketch, "E357.MirrorP", {"position": v(227.3, -149.28) * mm});
            skLineSegment(sketch, "E358.MirrorCS", {"start": v(541.68, 214.86) * mm, "end": v(224.22, 147.96) * mm});
            skPoint(sketch, "E359.MirrorP", {"position": v(543.23, 215.2) * mm});
            skLineSegment(sketch, "E360.MirrorCS", {"start": v(699.44, 304.58) * mm, "end": v(440.17, 87.48) * mm});
            skPoint(sketch, "E361.MirrorP", {"position": v(283.84, -202.43) * mm});
            skPoint(sketch, "E362.MirrorP", {"position": v(154.84, -190.55) * mm});
            skLineSegment(sketch, "E363.MirrorCS", {"start": v(283.44, -235.96) * mm, "end": v(155.15, -190.66) * mm});
            skPoint(sketch, "E364.MirrorP", {"position": v(325.87, 136.93) * mm});
            skPoint(sketch, "E365.MirrorP", {"position": v(194.12, 125.4) * mm});
            skLineSegment(sketch, "E366.MirrorCS", {"start": v(623.69, -549.09) * mm, "end": v(285.63, -237.28) * mm});
            skLineSegment(sketch, "E367.MirrorCS", {"start": v(442.3, -94.97) * mm, "end": v(696.3, -541.28) * mm});
            skPoint(sketch, "E368.MirrorP", {"position": v(418.88, -117.99) * mm});
            skLineSegment(sketch, "E369.MirrorCS", {"start": v(223.25, 112.73) * mm, "end": v(168.6, -3.82) * mm});
            skPoint(sketch, "E370.MirrorP", {"position": v(138.32, 6.37) * mm});
            skPoint(sketch, "E371.MirrorP", {"position": v(163.9, -160.08) * mm});
            skPoint(sketch, "E372.MirrorP", {"position": v(284.67, -236.4) * mm});
            skPoint(sketch, "E373.MirrorP", {"position": v(311.55, -218) * mm});
            skPoint(sketch, "E374.MirrorP", {"position": v(409.66, -87.59) * mm});
            skLineSegment(sketch, "E375.MirrorCS", {"start": v(437.9, 82.49) * mm, "end": v(441.48, -91.96) * mm});
            skLineSegment(sketch, "E376.MirrorCS", {"start": v(323.36, 136.4) * mm, "end": v(227.69, 116.24) * mm});
            skPoint(sketch, "E377.MirrorP", {"position": v(441.51, -93.57) * mm});
            skLineSegment(sketch, "E378", {"start": v(-478.65, 363.63) * mm, "end": v(-478.65, 348.25) * mm});
            skLineSegment(sketch, "E379", {"start": v(-481.83, 342.75) * mm, "end": v(-494.53, 335.41) * mm});
            skLineSegment(sketch, "E380.trimOffspring", {"start": v(-497.7, 363.63) * mm, "end": v(-497.7, 382.68) * mm});
            skPoint(sketch, "E381.visualSharp", {"position": v(-497.7, 333.58) * mm});
            skArc(sketch, "E381.filletArc", {"start": v(-494.53, 335.41) * mm, "mid": v(-496.85, 333.1) * mm, "end": v(-497.7, 329.92) * mm});
            skPoint(sketch, "E382.visualSharp", {"position": v(-478.65, 344.58) * mm});
            skArc(sketch, "E382.filletArc", {"start": v(-481.83, 342.75) * mm, "mid": v(-479.5, 345.07) * mm, "end": v(-478.65, 348.25) * mm});
            skLineSegment(sketch, "E383.trimOffspring", {"start": v(669.96, 382.68) * mm, "end": v(701.71, 382.68) * mm});
            skLineSegment(sketch, "E384", {"start": v(25.68, 230.28) * mm, "end": v(25.68, 249.33) * mm});
            skLineSegment(sketch, "E385", {"start": v(8.08, 249.33) * mm, "end": v(-9.52, 249.33) * mm});
            skLineSegment(sketch, "E386", {"start": v(-9.52, 249.33) * mm, "end": v(-9.52, 230.28) * mm});
            skLineSegment(sketch, "E387", {"start": v(146.57, 230.28) * mm, "end": v(146.57, 249.33) * mm});
            skLineSegment(sketch, "E388", {"start": v(164.17, 249.33) * mm, "end": v(181.78, 249.33) * mm});
            skLineSegment(sketch, "E389", {"start": v(181.78, 249.33) * mm, "end": v(181.78, 230.28) * mm});
            skLineSegment(sketch, "E390", {"start": v(669.96, 363.63) * mm, "end": v(650.91, 363.63) * mm});
            skLineSegment(sketch, "E391", {"start": v(650.91, 363.63) * mm, "end": v(650.91, 348.25) * mm});
            skLineSegment(sketch, "E392", {"start": v(654.09, 342.75) * mm, "end": v(666.79, 335.41) * mm});
            skLineSegment(sketch, "E393.trimOffspring", {"start": v(669.96, 363.63) * mm, "end": v(669.96, 382.68) * mm});
            skPoint(sketch, "E394.visualSharp", {"position": v(650.91, 344.58) * mm});
            skArc(sketch, "E394.filletArc", {"start": v(650.91, 348.25) * mm, "mid": v(651.76, 345.07) * mm, "end": v(654.09, 342.75) * mm});
            skPoint(sketch, "E395.visualSharp", {"position": v(669.96, 333.58) * mm});
            skArc(sketch, "E395.filletArc", {"start": v(669.96, 329.92) * mm, "mid": v(669.1, 333.1) * mm, "end": v(666.79, 335.41) * mm});
            skPoint(sketch, "E396.visualSharp", {"position": v(625.51, -550.77) * mm});
            skArc(sketch, "E396.filletArc", {"start": v(623.69, -549.09) * mm, "mid": v(625.68, -550.33) * mm, "end": v(628, -550.77) * mm});
            skPoint(sketch, "E397.visualSharp", {"position": v(701.71, -550.77) * mm});
            skArc(sketch, "E397.filletArc", {"start": v(690.8, -550.77) * mm, "mid": v(696.28, -547.61) * mm, "end": v(696.3, -541.28) * mm});
            skPoint(sketch, "E398.visualSharp", {"position": v(-529.45, -550.77) * mm});
            skArc(sketch, "E398.filletArc", {"start": v(-524.05, -541.28) * mm, "mid": v(-524.02, -547.61) * mm, "end": v(-518.53, -550.77) * mm});
            skPoint(sketch, "E399.visualSharp", {"position": v(-453.25, -550.77) * mm});
            skArc(sketch, "E399.filletArc", {"start": v(-455.73, -550.77) * mm, "mid": v(-453.42, -550.33) * mm, "end": v(-451.43, -549.09) * mm});
            skLineSegment(sketch, "E400", {"start": v(86.13, -0.17) * mm, "end": v(86.13, -34.56) * mm, "construction": true});
            skLineSegment(sketch, "E401", {"start": v(86.13, -150.07) * mm, "end": v(86.13, -182.74) * mm, "construction": true});
            skLineSegment(sketch, "E402", {"start": v(137.15, -28.5) * mm, "end": v(122.59, -34.56) * mm});
            skLineSegment(sketch, "E403", {"start": v(109.25, -34.56) * mm, "end": v(109.25, -17.36) * mm});
            skLineSegment(sketch, "E404", {"start": v(63, -34.56) * mm, "end": v(49.67, -34.56) * mm});
            skLineSegment(sketch, "E405", {"start": v(76.6, -0.17) * mm, "end": v(49.67, -0.17) * mm});
            skLineSegment(sketch, "E406", {"start": v(35.1, -28.5) * mm, "end": v(49.67, -34.56) * mm});
            skPoint(sketch, "E407", {"position": v(122.58, -17.36) * mm});
            skLineSegment(sketch, "E408", {"start": v(90.2, -17.36) * mm, "end": v(82.06, -17.36) * mm});
            skLineSegment(sketch, "E409", {"start": v(63.01, -182.74) * mm, "end": v(49.67, -182.74) * mm});
            skLineSegment(sketch, "E410", {"start": v(63, -150.07) * mm, "end": v(49.67, -150.07) * mm});
            skPoint(sketch, "E411", {"position": v(122.59, -166.4) * mm});
            skLineSegment(sketch, "E412", {"start": v(584, 249.33) * mm, "end": v(584, 230.28) * mm});
            skLineSegment(sketch, "E413.trimOffspring", {"start": v(561.25, 230.28) * mm, "end": v(544.45, 216.2) * mm});
            skLineSegment(sketch, "E414", {"start": v(584, 230.28) * mm, "end": v(561.25, 230.28) * mm});
            skLineSegment(sketch, "E415", {"start": v(-411.75, 249.33) * mm, "end": v(-411.75, 230.28) * mm});
            skLineSegment(sketch, "E416", {"start": v(-411.75, 230.28) * mm, "end": v(-389, 230.28) * mm});
            skLineSegment(sketch, "E417.trimOffspring", {"start": v(-389, 230.28) * mm, "end": v(-372.19, 216.2) * mm});
            skPoint(sketch, "E418", {"position": v(164.17, 249.33) * mm});
            skPoint(sketch, "E419", {"position": v(8.08, 249.33) * mm});
            skLineSegment(sketch, "E420.0", {"start": v(141.72, 249.33) * mm, "end": v(256.02, 363.63) * mm});
            skLineSegment(sketch, "E421", {"start": v(300.93, 363.63) * mm, "end": v(300.93, 382.68) * mm});
            skLineSegment(sketch, "E422", {"start": v(256.02, 363.63) * mm, "end": v(256.02, 382.68) * mm});
            skLineSegment(sketch, "E423", {"start": v(256.02, 382.68) * mm, "end": v(300.93, 382.68) * mm});
            skLineSegment(sketch, "E424", {"start": v(141.72, 249.33) * mm, "end": v(146.57, 249.33) * mm});
            skLineSegment(sketch, "E425", {"start": v(181.78, 249.33) * mm, "end": v(186.63, 249.33) * mm});
            skLineSegment(sketch, "E426.trimOffspring", {"start": v(186.63, 249.33) * mm, "end": v(300.93, 363.63) * mm});
            skLineSegment(sketch, "E427", {"start": v(164.17, 249.33) * mm, "end": v(164.17, 230.28) * mm});
            skLineSegment(sketch, "E428.trimOffspring", {"start": v(146.57, 249.33) * mm, "end": v(25.68, 249.33) * mm, "construction": true});
            skLineSegment(sketch, "E429.0", {"start": v(-14.37, 249.33) * mm, "end": v(-128.67, 363.63) * mm});
            skLineSegment(sketch, "E430.0", {"start": v(30.53, 249.33) * mm, "end": v(-83.77, 363.63) * mm});
            skLineSegment(sketch, "E431", {"start": v(30.53, 249.33) * mm, "end": v(25.68, 249.33) * mm});
            skLineSegment(sketch, "E432", {"start": v(-9.52, 249.33) * mm, "end": v(-14.37, 249.33) * mm});
            skLineSegment(sketch, "E433", {"start": v(-128.67, 363.63) * mm, "end": v(-128.67, 382.68) * mm});
            skLineSegment(sketch, "E434", {"start": v(-83.77, 363.63) * mm, "end": v(-83.77, 382.68) * mm});
            skLineSegment(sketch, "E435", {"start": v(-83.77, 382.68) * mm, "end": v(-128.67, 382.68) * mm});
            skLineSegment(sketch, "E436", {"start": v(49.67, -150.07) * mm, "end": v(49.67, -182.74) * mm, "construction": true});
            skLineSegment(sketch, "E437", {"start": v(49.67, -0.17) * mm, "end": v(49.67, -34.56) * mm, "construction": true});
            skLineSegment(sketch, "E438", {"start": v(8.08, 249.33) * mm, "end": v(8.08, 230.28) * mm});
            skPoint(sketch, "E439.orphan", {"position": v(122.58, -34.56) * mm});
            skLineSegment(sketch, "E440", {"start": v(122.58, -0.17) * mm, "end": v(76.6, -0.17) * mm});
            skLineSegment(sketch, "E441", {"start": v(109.25, -150.07) * mm, "end": v(122.59, -150.07) * mm});
            skLineSegment(sketch, "E442", {"start": v(122.59, -182.74) * mm, "end": v(109.25, -182.74) * mm});
            skLineSegment(sketch, "E443", {"start": v(63, -34.56) * mm, "end": v(63, -17.36) * mm});
            skLineSegment(sketch, "E444", {"start": v(122.59, -34.56) * mm, "end": v(109.25, -34.56) * mm});
            skLineSegment(sketch, "E445.trimOffspring", {"start": v(63, -0.17) * mm, "end": v(63, 0) * mm});
            skLineSegment(sketch, "E446", {"start": v(63, -150.07) * mm, "end": v(72.53, -150.07) * mm});
            skPoint(sketch, "E447.orphan", {"position": v(82.06, -150.07) * mm});
            skLineSegment(sketch, "E448", {"start": v(63.01, -182.74) * mm, "end": v(82.06, -182.74) * mm});
            skLineSegment(sketch, "E449", {"start": v(82.06, -182.74) * mm, "end": v(82.06, -150.07) * mm});
            skLineSegment(sketch, "E450", {"start": v(82.06, -150.07) * mm, "end": v(63, -150.07) * mm});
            skLineSegment(sketch, "E451", {"start": v(109.25, -150.07) * mm, "end": v(90.2, -150.07) * mm});
            skLineSegment(sketch, "E452", {"start": v(90.2, -150.07) * mm, "end": v(90.2, -182.74) * mm});
            skLineSegment(sketch, "E453", {"start": v(109.25, -182.74) * mm, "end": v(90.2, -182.74) * mm});
            skLineSegment(sketch, "E454", {"start": v(82.06, -34.56) * mm, "end": v(82.06, -17.36) * mm});
            skLineSegment(sketch, "E455", {"start": v(90.2, -34.56) * mm, "end": v(90.2, -17.36) * mm});
            skLineSegment(sketch, "E456", {"start": v(63, -34.56) * mm, "end": v(82.06, -34.56) * mm});
            skLineSegment(sketch, "E457.trimOffspring", {"start": v(90.2, -34.56) * mm, "end": v(109.25, -34.56) * mm});
            skSolve(sketch);
        }
        {
            var Q0;
            Q0=qCreatedBy(makeId("Front.planeOp"),FACE);
            var sketch = newSketch(context, id + "F5", { "sketchPlane" : qUnion([Q0])});
            skLineSegment(sketch, "E458.bottom", {"start": v(-726.25, -550.77) * mm, "end": v(-663.45, -550.77) * mm});
            skLineSegment(sketch, "E458.top", {"start": v(-737.17, 382.68) * mm, "end": v(-705.42, 382.68) * mm});
            skLineSegment(sketch, "E459", {"start": v(-705.42, 363.63) * mm, "end": v(-686.37, 363.63) * mm});
            skLineSegment(sketch, "E460", {"start": v(-734.9, 304.57) * mm, "end": v(-475.64, 87.48) * mm});
            skLineSegment(sketch, "E461", {"start": v(-473.37, 82.48) * mm, "end": v(-476.94, -91.96) * mm});
            skLineSegment(sketch, "E462", {"start": v(-477.77, -94.97) * mm, "end": v(-731.77, -541.28) * mm});
            skLineSegment(sketch, "E463", {"start": v(-726.25, -550.77) * mm, "end": v(-660.97, -550.77) * mm});
            skLineSegment(sketch, "E464", {"start": v(-659.15, -549.1) * mm, "end": v(-321.1, -237.28) * mm});
            skLineSegment(sketch, "E465", {"start": v(-318.9, -235.96) * mm, "end": v(-190.61, -190.66) * mm});
            skLineSegment(sketch, "E466", {"start": v(-190, -190.48) * mm, "end": v(-158.05, -182.74) * mm});
            skLineSegment(sketch, "E467", {"start": v(-181, 230.29) * mm, "end": v(-227.34, 128.07) * mm});
            skLineSegment(sketch, "E468", {"start": v(-227.31, 122.75) * mm, "end": v(-173.8, 8.6) * mm});
            skLineSegment(sketch, "E469", {"start": v(-170.48, 5.43) * mm, "end": v(-157.02, -0.16) * mm});
            skLineSegment(sketch, "E470.0", {"start": v(-662.7, -509.17) * mm, "end": v(-350.52, -221.23) * mm});
            skLineSegment(sketch, "E471.0", {"start": v(-456.93, -122.54) * mm, "end": v(-672.52, -501.36) * mm});
            skLineSegment(sketch, "E472.0", {"start": v(-199.04, -160) * mm, "end": v(-158.05, -150.07) * mm});
            skLineSegment(sketch, "E472.1", {"start": v(-314, -200.56) * mm, "end": v(-280.57, -188.76) * mm});
            skLineSegment(sketch, "E473.1", {"start": v(-258.71, 112.72) * mm, "end": v(-204.07, -3.82) * mm});
            skLineSegment(sketch, "E474.0", {"start": v(-705.42, 324.27) * mm, "end": v(-705.42, 329.91) * mm});
            skLineSegment(sketch, "E475.0", {"start": v(-703.15, 319.4) * mm, "end": v(-619.47, 249.33) * mm});
            skLineSegment(sketch, "E476.0", {"start": v(-441.6, 83.27) * mm, "end": v(-445.01, -83.54) * mm});
            skLineSegment(sketch, "E477.0", {"start": v(-502.03, 166.58) * mm, "end": v(-421.48, 149.6) * mm});
            skLineSegment(sketch, "E478.0", {"start": v(-577.14, 214.86) * mm, "end": v(-259.68, 147.96) * mm});
            skLineSegment(sketch, "E479.0", {"start": v(-438.61, 88.52) * mm, "end": v(-363.5, 135.57) * mm});
            skLineSegment(sketch, "E480.0", {"start": v(-453.9, 116.41) * mm, "end": v(-419.42, 138.01) * mm});
            skLineSegment(sketch, "E481.0", {"start": v(-440.71, -89.08) * mm, "end": v(-298.6, -137.16) * mm});
            skLineSegment(sketch, "E482.0", {"start": v(-449.38, -119.67) * mm, "end": v(-387.59, -140.57) * mm});
            skLineSegment(sketch, "E483.0", {"start": v(-321.8, -197.4) * mm, "end": v(-335.62, -169.6) * mm});
            skLineSegment(sketch, "E484.0", {"start": v(-349.14, -213.73) * mm, "end": v(-383.94, -143.76) * mm});
            skLineSegment(sketch, "E485.0", {"start": v(-204.6, -10.14) * mm, "end": v(-291.34, -134.78) * mm});
            skLineSegment(sketch, "E486.0", {"start": v(-180.26, -30.74) * mm, "end": v(-257.93, -142.35) * mm});
            skLineSegment(sketch, "E487.trimOffspring", {"start": v(-507.41, 155.5) * mm, "end": v(-461.35, 116.93) * mm});
            skLineSegment(sketch, "E488.trimOffspring", {"start": v(-358.82, 136.4) * mm, "end": v(-263.15, 116.24) * mm});
            skLineSegment(sketch, "E489.trimOffspring", {"start": v(-254.76, -152) * mm, "end": v(-216.85, -164.82) * mm});
            skLineSegment(sketch, "E490.trimOffspring", {"start": v(-327.9, -160.77) * mm, "end": v(-280.65, -176.75) * mm});
            skLineSegment(sketch, "E491", {"start": v(-199.64, 230.29) * mm, "end": v(-181, 230.29) * mm});
            skPoint(sketch, "E492.orphan", {"position": v(-120.56, 363.64) * mm});
            skLineSegment(sketch, "E493.trimOffspring", {"start": v(-218.27, 230.29) * mm, "end": v(-252.55, 151.63) * mm});
            skPoint(sketch, "E494.visualSharp", {"position": v(-319.3, -202.43) * mm});
            skArc(sketch, "E494.filletArc", {"start": v(-321.8, -197.4) * mm, "mid": v(-318.5, -200.46) * mm, "end": v(-314, -200.56) * mm});
            skLineSegment(sketch, "E495.trimOffspring", {"start": v(-212.7, -164.8) * mm, "end": v(-199.66, -160.19) * mm});
            skPoint(sketch, "E496.visualSharp", {"position": v(-342.47, -155.84) * mm});
            skArc(sketch, "E496.filletArc", {"start": v(-327.9, -160.77) * mm, "mid": v(-334.72, -162.6) * mm, "end": v(-335.62, -169.6) * mm});
            skPoint(sketch, "E497.visualSharp", {"position": v(-263.25, -182.64) * mm});
            skArc(sketch, "E497.filletArc", {"start": v(-280.57, -188.76) * mm, "mid": v(-276.33, -182.73) * mm, "end": v(-280.65, -176.75) * mm});
            skPoint(sketch, "E498.visualSharp", {"position": v(-347.02, -218) * mm});
            skArc(sketch, "E498.filletArc", {"start": v(-350.52, -221.23) * mm, "mid": v(-348.58, -217.71) * mm, "end": v(-349.14, -213.73) * mm});
            skPoint(sketch, "E499.visualSharp", {"position": v(-385.1, -141.41) * mm});
            skArc(sketch, "E499.filletArc", {"start": v(-383.94, -143.76) * mm, "mid": v(-385.45, -141.8) * mm, "end": v(-387.59, -140.57) * mm});
            skPoint(sketch, "E500.visualSharp", {"position": v(-454.34, -117.99) * mm});
            skArc(sketch, "E500.filletArc", {"start": v(-449.38, -119.67) * mm, "mid": v(-453.67, -119.75) * mm, "end": v(-456.93, -122.54) * mm});
            skPoint(sketch, "E501.visualSharp", {"position": v(-692.73, -536.87) * mm});
            skArc(sketch, "E501.filletArc", {"start": v(-672.52, -501.36) * mm, "mid": v(-670.95, -509.47) * mm, "end": v(-662.7, -509.17) * mm});
            skPoint(sketch, "E502.visualSharp", {"position": v(-445.12, -87.59) * mm});
            skArc(sketch, "E502.filletArc", {"start": v(-445.03, -82.94) * mm, "mid": v(-443.88, -86.71) * mm, "end": v(-440.71, -89.08) * mm});
            skPoint(sketch, "E503.visualSharp", {"position": v(-294.07, -138.7) * mm});
            skArc(sketch, "E503.filletArc", {"start": v(-298.6, -137.16) * mm, "mid": v(-294.57, -137.18) * mm, "end": v(-291.34, -134.78) * mm});
            skPoint(sketch, "E504.visualSharp", {"position": v(-262.76, -149.29) * mm});
            skArc(sketch, "E504.filletArc", {"start": v(-257.93, -142.35) * mm, "mid": v(-258.75, -147.97) * mm, "end": v(-254.76, -152) * mm});
            skPoint(sketch, "E505.visualSharp", {"position": v(-214.77, -165.52) * mm});
            skArc(sketch, "E505.filletArc", {"start": v(-216.85, -164.82) * mm, "mid": v(-214.77, -165.15) * mm, "end": v(-212.7, -164.8) * mm});
            skPoint(sketch, "E506.visualSharp", {"position": v(-199.36, -160.08) * mm});
            skArc(sketch, "E506.filletArc", {"start": v(-199.04, -160) * mm, "mid": v(-199.35, -160.09) * mm, "end": v(-199.66, -160.19) * mm});
            skPoint(sketch, "E507.visualSharp", {"position": v(-190.3, -190.56) * mm});
            skArc(sketch, "E507.filletArc", {"start": v(-190, -190.48) * mm, "mid": v(-190.3, -190.57) * mm, "end": v(-190.61, -190.66) * mm});
            skPoint(sketch, "E508.visualSharp", {"position": v(-320.14, -236.4) * mm});
            skArc(sketch, "E508.filletArc", {"start": v(-318.9, -235.96) * mm, "mid": v(-320.07, -236.51) * mm, "end": v(-321.1, -237.28) * mm});
            skPoint(sketch, "E509.visualSharp", {"position": v(-177.34, -26.54) * mm});
            skArc(sketch, "E509.filletArc", {"start": v(-172.61, -28.5) * mm, "mid": v(-176.83, -28.27) * mm, "end": v(-180.26, -30.74) * mm});
            skPoint(sketch, "E510.visualSharp", {"position": v(-172.75, 6.37) * mm});
            skArc(sketch, "E510.filletArc", {"start": v(-173.8, 8.6) * mm, "mid": v(-172.43, 6.7) * mm, "end": v(-170.48, 5.43) * mm});
            skPoint(sketch, "E511.visualSharp", {"position": v(-202.52, -7.14) * mm});
            skArc(sketch, "E511.filletArc", {"start": v(-204.6, -10.14) * mm, "mid": v(-203.5, -7.05) * mm, "end": v(-204.07, -3.82) * mm});
            skPoint(sketch, "E512.visualSharp", {"position": v(-476.97, -93.57) * mm});
            skArc(sketch, "E512.filletArc", {"start": v(-477.77, -94.97) * mm, "mid": v(-477.17, -93.52) * mm, "end": v(-476.94, -91.96) * mm});
            skPoint(sketch, "E513.visualSharp", {"position": v(-473.3, 85.53) * mm});
            skArc(sketch, "E513.filletArc", {"start": v(-473.37, 82.48) * mm, "mid": v(-473.93, 85.24) * mm, "end": v(-475.64, 87.48) * mm});
            skPoint(sketch, "E514.visualSharp", {"position": v(-441.52, 86.7) * mm});
            skArc(sketch, "E514.filletArc", {"start": v(-438.61, 88.52) * mm, "mid": v(-440.77, 86.27) * mm, "end": v(-441.6, 83.27) * mm});
            skPoint(sketch, "E515.visualSharp", {"position": v(-457.8, 113.96) * mm});
            skArc(sketch, "E515.filletArc", {"start": v(-461.35, 116.93) * mm, "mid": v(-457.7, 115.46) * mm, "end": v(-453.9, 116.41) * mm});
            skPoint(sketch, "E516.visualSharp", {"position": v(-260.05, 115.59) * mm});
            skArc(sketch, "E516.filletArc", {"start": v(-258.71, 112.72) * mm, "mid": v(-260.52, 115) * mm, "end": v(-263.15, 116.24) * mm});
            skPoint(sketch, "E517.visualSharp", {"position": v(-361.33, 136.93) * mm});
            skArc(sketch, "E517.filletArc", {"start": v(-358.82, 136.4) * mm, "mid": v(-361.25, 136.44) * mm, "end": v(-363.5, 135.57) * mm});
            skPoint(sketch, "E518.visualSharp", {"position": v(-406.09, 146.36) * mm});
            skArc(sketch, "E518.filletArc", {"start": v(-419.42, 138.01) * mm, "mid": v(-416.54, 144.5) * mm, "end": v(-421.48, 149.6) * mm});
            skPoint(sketch, "E519.visualSharp", {"position": v(-254.62, 146.89) * mm});
            skArc(sketch, "E519.filletArc", {"start": v(-259.68, 147.96) * mm, "mid": v(-255.46, 148.53) * mm, "end": v(-252.55, 151.63) * mm});
            skPoint(sketch, "E520.visualSharp", {"position": v(-228.55, 125.4) * mm});
            skArc(sketch, "E520.filletArc", {"start": v(-227.34, 128.07) * mm, "mid": v(-227.91, 125.4) * mm, "end": v(-227.31, 122.75) * mm});
            skPoint(sketch, "E521.visualSharp", {"position": v(-526.91, 171.83) * mm});
            skArc(sketch, "E521.filletArc", {"start": v(-502.03, 166.58) * mm, "mid": v(-509.05, 163.14) * mm, "end": v(-507.41, 155.5) * mm});
            skPoint(sketch, "E522.visualSharp", {"position": v(-578.7, 215.19) * mm});
            skArc(sketch, "E522.filletArc", {"start": v(-579.91, 216.2) * mm, "mid": v(-578.6, 215.36) * mm, "end": v(-577.14, 214.86) * mm});
            skLineSegment(sketch, "E523", {"start": v(-737.17, 382.68) * mm, "end": v(-737.17, 309.44) * mm});
            skPoint(sketch, "E524.visualSharp", {"position": v(-737.17, 306.48) * mm});
            skArc(sketch, "E524.filletArc", {"start": v(-737.17, 309.44) * mm, "mid": v(-736.58, 306.76) * mm, "end": v(-734.9, 304.57) * mm});
            skPoint(sketch, "E525.visualSharp", {"position": v(-705.42, 321.3) * mm});
            skArc(sketch, "E525.filletArc", {"start": v(-705.42, 324.27) * mm, "mid": v(-704.83, 321.58) * mm, "end": v(-703.15, 319.4) * mm});
            skArc(sketch, "E526.MirrorCS", {"start": v(234.59, -94.97) * mm, "mid": v(233.98, -93.52) * mm, "end": v(233.76, -91.96) * mm});
            skArc(sketch, "E527.MirrorCS", {"start": v(195.43, 88.52) * mm, "mid": v(197.58, 86.27) * mm, "end": v(198.4, 83.27) * mm});
            skArc(sketch, "E528.MirrorCS", {"start": v(-26.34, -164.82) * mm, "mid": v(-28.41, -165.15) * mm, "end": v(-30.49, -164.8) * mm});
            skArc(sketch, "E529.MirrorCS", {"start": v(-44.14, -160) * mm, "mid": v(-43.83, -160.09) * mm, "end": v(-43.52, -160.19) * mm});
            skLineSegment(sketch, "E530.MirrorCS", {"start": v(-30.49, -164.8) * mm, "end": v(-43.52, -160.19) * mm});
            skArc(sketch, "E531.MirrorCS", {"start": v(230.18, 82.48) * mm, "mid": v(230.75, 85.24) * mm, "end": v(232.45, 87.48) * mm});
            skArc(sketch, "E532.MirrorCS", {"start": v(75.72, -235.96) * mm, "mid": v(76.88, -236.51) * mm, "end": v(77.91, -237.28) * mm});
            skLineSegment(sketch, "E533.MirrorCS", {"start": v(78.62, -197.4) * mm, "end": v(92.44, -169.6) * mm});
            skArc(sketch, "E534.MirrorCS", {"start": v(-70.57, -28.5) * mm, "mid": v(-66.35, -28.27) * mm, "end": v(-62.92, -30.74) * mm});
            skArc(sketch, "E535.MirrorCS", {"start": v(-53.2, -190.48) * mm, "mid": v(-52.88, -190.57) * mm, "end": v(-52.57, -190.66) * mm});
            skArc(sketch, "E536.MirrorCS", {"start": v(115.64, 136.4) * mm, "mid": v(118.06, 136.44) * mm, "end": v(120.32, 135.57) * mm});
            skArc(sketch, "E537.MirrorCS", {"start": v(78.62, -197.4) * mm, "mid": v(75.32, -200.46) * mm, "end": v(70.82, -200.56) * mm});
            skArc(sketch, "E538.MirrorCS", {"start": v(84.72, -160.77) * mm, "mid": v(91.54, -162.6) * mm, "end": v(92.44, -169.6) * mm});
            skArc(sketch, "E539.MirrorCS", {"start": v(336.73, 216.2) * mm, "mid": v(335.43, 215.36) * mm, "end": v(333.96, 214.86) * mm});
            skArc(sketch, "E540.MirrorCS", {"start": v(15.53, 112.72) * mm, "mid": v(17.33, 115) * mm, "end": v(19.97, 116.24) * mm});
            skArc(sketch, "E541.MirrorCS", {"start": v(462.24, 324.27) * mm, "mid": v(461.64, 321.58) * mm, "end": v(459.97, 319.4) * mm});
            skArc(sketch, "E542.MirrorCS", {"start": v(218.16, 116.93) * mm, "mid": v(214.52, 115.46) * mm, "end": v(210.71, 116.41) * mm});
            skArc(sketch, "E543.MirrorCS", {"start": v(140.75, -143.76) * mm, "mid": v(142.26, -141.8) * mm, "end": v(144.4, -140.57) * mm});
            skArc(sketch, "E544.MirrorCS", {"start": v(16.5, 147.96) * mm, "mid": v(12.3, 148.5) * mm, "end": v(9.4, 151.57) * mm});
            skArc(sketch, "E545.MirrorCS", {"start": v(-66.8, 8.6) * mm, "mid": v(-68.15, 6.7) * mm, "end": v(-70.1, 5.43) * mm});
            skArc(sketch, "E546.MirrorCS", {"start": v(107.33, -221.23) * mm, "mid": v(105.4, -217.71) * mm, "end": v(105.95, -213.73) * mm});
            skArc(sketch, "E547.MirrorCS", {"start": v(55.4, -137.16) * mm, "mid": v(51.38, -137.18) * mm, "end": v(48.16, -134.78) * mm});
            skLineSegment(sketch, "E548.MirrorCS", {"start": v(210.71, 116.41) * mm, "end": v(176.23, 138.01) * mm});
            skArc(sketch, "E549.MirrorCS", {"start": v(-13.24, 128.07) * mm, "mid": v(-12.68, 125.4) * mm, "end": v(-13.28, 122.75) * mm});
            skArc(sketch, "E550.MirrorCS", {"start": v(176.23, 138.01) * mm, "mid": v(173.35, 144.5) * mm, "end": v(178.3, 149.6) * mm});
            skArc(sketch, "E551.MirrorCS", {"start": v(201.84, -82.94) * mm, "mid": v(200.7, -86.71) * mm, "end": v(197.53, -89.08) * mm});
            skArc(sketch, "E552.MirrorCS", {"start": v(206.2, -119.67) * mm, "mid": v(210.48, -119.75) * mm, "end": v(213.75, -122.54) * mm});
            skArc(sketch, "E553.MirrorCS", {"start": v(493.99, 309.44) * mm, "mid": v(493.4, 306.76) * mm, "end": v(491.72, 304.57) * mm});
            skArc(sketch, "E554.MirrorCS", {"start": v(258.84, 166.58) * mm, "mid": v(265.86, 163.14) * mm, "end": v(264.23, 155.5) * mm});
            skLineSegment(sketch, "E555.MirrorCS", {"start": v(11.57, -152) * mm, "end": v(-26.34, -164.82) * mm});
            skLineSegment(sketch, "E556.MirrorCS", {"start": v(493.99, -550.77) * mm, "end": v(417.79, -550.77) * mm});
            skLineSegment(sketch, "E557.MirrorCS", {"start": v(70.82, -200.56) * mm, "end": v(37.38, -188.76) * mm});
            skArc(sketch, "E558.MirrorCS", {"start": v(429.34, -501.36) * mm, "mid": v(427.77, -509.47) * mm, "end": v(419.51, -509.17) * mm});
            skLineSegment(sketch, "E559.MirrorCS", {"start": v(84.72, -160.77) * mm, "end": v(37.46, -176.75) * mm});
            skArc(sketch, "E560.MirrorCS", {"start": v(37.38, -188.76) * mm, "mid": v(33.15, -182.73) * mm, "end": v(37.46, -176.75) * mm});
            skArc(sketch, "E561.MirrorCS", {"start": v(14.75, -142.35) * mm, "mid": v(15.57, -147.97) * mm, "end": v(11.57, -152) * mm});
            skArc(sketch, "E562.MirrorCS", {"start": v(-38.58, -10.14) * mm, "mid": v(-39.7, -7.05) * mm, "end": v(-39.11, -3.82) * mm});
            skLineSegment(sketch, "E563.MirrorCS", {"start": v(105.95, -213.73) * mm, "end": v(140.75, -143.76) * mm});
            skLineSegment(sketch, "E564.MirrorCS", {"start": v(-42.76, 230.28) * mm, "end": v(-59.58, 230.29) * mm});
            skLineSegment(sketch, "E565.MirrorCS", {"start": v(264.23, 155.5) * mm, "end": v(218.16, 116.93) * mm});
            skLineSegment(sketch, "E566.MirrorCS", {"start": v(462.24, 324.27) * mm, "end": v(462.24, 329.91) * mm});
            skLineSegment(sketch, "E567.MirrorCS", {"start": v(483.07, -550.77) * mm, "end": v(420.27, -550.77) * mm});
            skLineSegment(sketch, "E568.MirrorCS", {"start": v(-70.1, 5.43) * mm, "end": v(-83.56, -0.16) * mm});
            skPoint(sketch, "E569.MirrorP", {"position": v(-28.42, -165.52) * mm});
            skLineSegment(sketch, "E570.MirrorCS", {"start": v(-38.58, -10.14) * mm, "end": v(48.16, -134.78) * mm});
            skLineSegment(sketch, "E571.MirrorCS", {"start": v(258.84, 166.58) * mm, "end": v(178.3, 149.6) * mm});
            skPoint(sketch, "E572.MirrorP", {"position": v(99.29, -155.84) * mm});
            skPoint(sketch, "E573.MirrorP", {"position": v(-65.85, -26.54) * mm});
            skPoint(sketch, "E574.MirrorP", {"position": v(162.9, 146.36) * mm});
            skPoint(sketch, "E575.MirrorP", {"position": v(198.34, 86.7) * mm});
            skLineSegment(sketch, "E576.MirrorCS", {"start": v(-62.92, -30.74) * mm, "end": v(14.75, -142.35) * mm});
            skLineSegment(sketch, "E577.MirrorCS", {"start": v(206.2, -119.67) * mm, "end": v(144.4, -140.57) * mm});
            skLineSegment(sketch, "E578.MirrorCS", {"start": v(195.43, 88.52) * mm, "end": v(120.32, 135.57) * mm});
            skPoint(sketch, "E579.MirrorP", {"position": v(50.89, -138.7) * mm});
            skLineSegment(sketch, "E580.MirrorCS", {"start": v(-44.14, -160) * mm, "end": v(-85.13, -150.07) * mm});
            skLineSegment(sketch, "E581.MirrorCS", {"start": v(-53.2, -190.48) * mm, "end": v(-85.13, -182.74) * mm});
            skLineSegment(sketch, "E582.MirrorCS", {"start": v(197.53, -89.08) * mm, "end": v(55.4, -137.16) * mm});
            skPoint(sketch, "E583.MirrorP", {"position": v(462.24, 321.3) * mm});
            skPoint(sketch, "E584.MirrorP", {"position": v(16.87, 115.59) * mm});
            skPoint(sketch, "E585.MirrorP", {"position": v(-40.67, -7.14) * mm});
            skPoint(sketch, "E586.MirrorP", {"position": v(11.49, 146.9) * mm});
            skLineSegment(sketch, "E587.MirrorCS", {"start": v(-25.94, 230.28) * mm, "end": v(9.4, 151.57) * mm});
            skLineSegment(sketch, "E588.MirrorCS", {"start": v(419.51, -509.17) * mm, "end": v(107.33, -221.23) * mm});
            skLineSegment(sketch, "E589.MirrorCS", {"start": v(-13.28, 122.75) * mm, "end": v(-66.8, 8.6) * mm});
            skLineSegment(sketch, "E590.MirrorCS", {"start": v(198.4, 83.27) * mm, "end": v(201.83, -83.54) * mm});
            skPoint(sketch, "E591.MirrorP", {"position": v(-121.6, 363.63) * mm});
            skLineSegment(sketch, "E592.MirrorCS", {"start": v(459.97, 319.4) * mm, "end": v(376.28, 249.33) * mm});
            skLineSegment(sketch, "E593.MirrorCS", {"start": v(493.99, 382.68) * mm, "end": v(493.99, 309.44) * mm});
            skPoint(sketch, "E594.MirrorP", {"position": v(20.06, -182.64) * mm});
            skPoint(sketch, "E595.MirrorP", {"position": v(214.62, 113.96) * mm});
            skLineSegment(sketch, "E596.MirrorCS", {"start": v(-59.58, 230.29) * mm, "end": v(-13.24, 128.07) * mm});
            skPoint(sketch, "E597.MirrorP", {"position": v(283.73, 171.83) * mm});
            skPoint(sketch, "E598.MirrorP", {"position": v(141.92, -141.41) * mm});
            skPoint(sketch, "E599.MirrorP", {"position": v(493.99, 306.48) * mm});
            skPoint(sketch, "E600.MirrorP", {"position": v(230.12, 85.53) * mm});
            skLineSegment(sketch, "E601.MirrorCS", {"start": v(213.75, -122.54) * mm, "end": v(429.34, -501.36) * mm});
            skPoint(sketch, "E602.MirrorP", {"position": v(19.58, -149.29) * mm});
            skLineSegment(sketch, "E603.MirrorCS", {"start": v(333.96, 214.86) * mm, "end": v(16.5, 147.96) * mm});
            skPoint(sketch, "E604.MirrorP", {"position": v(335.51, 215.19) * mm});
            skLineSegment(sketch, "E605.MirrorCS", {"start": v(491.72, 304.57) * mm, "end": v(232.45, 87.48) * mm});
            skPoint(sketch, "E606.MirrorP", {"position": v(76.11, -202.43) * mm});
            skPoint(sketch, "E607.MirrorP", {"position": v(-52.88, -190.56) * mm});
            skLineSegment(sketch, "E608.MirrorCS", {"start": v(75.72, -235.96) * mm, "end": v(-52.57, -190.66) * mm});
            skPoint(sketch, "E609.MirrorP", {"position": v(118.15, 136.93) * mm});
            skPoint(sketch, "E610.MirrorP", {"position": v(-13.6, 125.4) * mm});
            skLineSegment(sketch, "E611.MirrorCS", {"start": v(415.96, -549.1) * mm, "end": v(77.91, -237.28) * mm});
            skLineSegment(sketch, "E612.MirrorCS", {"start": v(234.59, -94.97) * mm, "end": v(488.59, -541.28) * mm});
            skPoint(sketch, "E613.MirrorP", {"position": v(211.15, -117.99) * mm});
            skLineSegment(sketch, "E614.MirrorCS", {"start": v(15.53, 112.72) * mm, "end": v(-39.11, -3.82) * mm});
            skPoint(sketch, "E615.MirrorP", {"position": v(-69.4, 6.37) * mm});
            skPoint(sketch, "E616.MirrorP", {"position": v(-43.83, -160.08) * mm});
            skPoint(sketch, "E617.MirrorP", {"position": v(76.95, -236.4) * mm});
            skPoint(sketch, "E618.MirrorP", {"position": v(103.83, -218) * mm});
            skPoint(sketch, "E619.MirrorP", {"position": v(201.94, -87.59) * mm});
            skLineSegment(sketch, "E620.MirrorCS", {"start": v(230.18, 82.48) * mm, "end": v(233.76, -91.96) * mm});
            skLineSegment(sketch, "E621.MirrorCS", {"start": v(115.64, 136.4) * mm, "end": v(19.97, 116.24) * mm});
            skPoint(sketch, "E622.MirrorP", {"position": v(233.79, -93.57) * mm});
            skLineSegment(sketch, "E623", {"start": v(-686.37, 363.63) * mm, "end": v(-686.37, 348.24) * mm});
            skLineSegment(sketch, "E624", {"start": v(-689.55, 342.74) * mm, "end": v(-702.25, 335.41) * mm});
            skLineSegment(sketch, "E625.trimOffspring", {"start": v(-705.42, 363.63) * mm, "end": v(-705.42, 382.68) * mm});
            skPoint(sketch, "E626.visualSharp", {"position": v(-705.42, 333.58) * mm});
            skArc(sketch, "E626.filletArc", {"start": v(-702.25, 335.41) * mm, "mid": v(-704.57, 333.09) * mm, "end": v(-705.42, 329.91) * mm});
            skPoint(sketch, "E627.visualSharp", {"position": v(-686.37, 344.58) * mm});
            skArc(sketch, "E627.filletArc", {"start": v(-689.55, 342.74) * mm, "mid": v(-687.22, 345.07) * mm, "end": v(-686.37, 348.24) * mm});
            skLineSegment(sketch, "E628.trimOffspring", {"start": v(462.24, 382.68) * mm, "end": v(493.99, 382.68) * mm});
            skLineSegment(sketch, "E629", {"start": v(-181, 230.29) * mm, "end": v(-181, 249.34) * mm});
            skLineSegment(sketch, "E630", {"start": v(-199.64, 249.34) * mm, "end": v(-218.27, 249.34) * mm});
            skLineSegment(sketch, "E631", {"start": v(-218.27, 249.34) * mm, "end": v(-218.27, 230.29) * mm});
            skLineSegment(sketch, "E632", {"start": v(-59.58, 230.29) * mm, "end": v(-59.58, 249.34) * mm});
            skLineSegment(sketch, "E633", {"start": v(-42.76, 249.34) * mm, "end": v(-25.94, 249.34) * mm});
            skLineSegment(sketch, "E634", {"start": v(-25.94, 249.34) * mm, "end": v(-25.94, 230.28) * mm});
            skLineSegment(sketch, "E635", {"start": v(462.24, 363.63) * mm, "end": v(443.19, 363.63) * mm});
            skLineSegment(sketch, "E636", {"start": v(443.19, 363.63) * mm, "end": v(443.19, 348.24) * mm});
            skLineSegment(sketch, "E637", {"start": v(446.36, 342.74) * mm, "end": v(459.06, 335.41) * mm});
            skLineSegment(sketch, "E638.trimOffspring", {"start": v(462.24, 363.63) * mm, "end": v(462.24, 382.68) * mm});
            skPoint(sketch, "E639.visualSharp", {"position": v(443.19, 344.58) * mm});
            skArc(sketch, "E639.filletArc", {"start": v(443.19, 348.24) * mm, "mid": v(444.04, 345.07) * mm, "end": v(446.36, 342.74) * mm});
            skPoint(sketch, "E640.visualSharp", {"position": v(462.24, 333.58) * mm});
            skArc(sketch, "E640.filletArc", {"start": v(462.24, 329.91) * mm, "mid": v(461.39, 333.09) * mm, "end": v(459.06, 335.41) * mm});
            skPoint(sketch, "E641.visualSharp", {"position": v(417.79, -550.77) * mm});
            skArc(sketch, "E641.filletArc", {"start": v(415.96, -549.1) * mm, "mid": v(417.96, -550.34) * mm, "end": v(420.27, -550.77) * mm});
            skPoint(sketch, "E642.visualSharp", {"position": v(493.99, -550.77) * mm});
            skArc(sketch, "E642.filletArc", {"start": v(483.07, -550.77) * mm, "mid": v(488.56, -547.62) * mm, "end": v(488.59, -541.28) * mm});
            skPoint(sketch, "E643.visualSharp", {"position": v(-737.17, -550.77) * mm});
            skArc(sketch, "E643.filletArc", {"start": v(-731.77, -541.28) * mm, "mid": v(-731.74, -547.62) * mm, "end": v(-726.25, -550.77) * mm});
            skPoint(sketch, "E644.visualSharp", {"position": v(-660.97, -550.77) * mm});
            skArc(sketch, "E644.filletArc", {"start": v(-663.45, -550.77) * mm, "mid": v(-661.14, -550.34) * mm, "end": v(-659.15, -549.1) * mm});
            skLineSegment(sketch, "E645", {"start": v(-121.6, -17.37) * mm, "end": v(-121.6, -34.56) * mm, "construction": true});
            skLineSegment(sketch, "E646", {"start": v(-121.6, -150.07) * mm, "end": v(-121.6, -182.74) * mm, "construction": true});
            skLineSegment(sketch, "E647", {"start": v(-70.57, -28.5) * mm, "end": v(-85.13, -34.56) * mm});
            skLineSegment(sketch, "E648", {"start": v(-85.13, -182.74) * mm, "end": v(-85.13, -150.07) * mm, "construction": true});
            skLineSegment(sketch, "E649.trimOffspring", {"start": v(-131.12, -150.07) * mm, "end": v(-131.12, -182.74) * mm, "construction": true});
            skLineSegment(sketch, "E650", {"start": v(-172.61, -28.5) * mm, "end": v(-158.05, -34.56) * mm});
            skPoint(sketch, "E651", {"position": v(-83.56, -17.36) * mm});
            skLineSegment(sketch, "E652", {"start": v(-116.83, -17.36) * mm, "end": v(-124.64, -17.36) * mm});
            skLineSegment(sketch, "E653", {"start": v(-131.12, -182.74) * mm, "end": v(-158.05, -182.74) * mm});
            skLineSegment(sketch, "E654", {"start": v(-131.12, -150.07) * mm, "end": v(-158.05, -150.07) * mm});
            skPoint(sketch, "E655", {"position": v(-85.13, -166.4) * mm});
            skLineSegment(sketch, "E656", {"start": v(-85.13, -166.4) * mm, "end": v(-131.12, -166.4) * mm});
            skLineSegment(sketch, "E657", {"start": v(376.28, 249.33) * mm, "end": v(376.28, 230.28) * mm});
            skLineSegment(sketch, "E658.trimOffspring", {"start": v(353.53, 230.28) * mm, "end": v(336.73, 216.2) * mm});
            skLineSegment(sketch, "E659", {"start": v(376.28, 230.28) * mm, "end": v(353.53, 230.28) * mm});
            skLineSegment(sketch, "E660", {"start": v(-619.47, 249.33) * mm, "end": v(-619.47, 230.28) * mm});
            skLineSegment(sketch, "E661", {"start": v(-619.47, 230.28) * mm, "end": v(-596.72, 230.28) * mm});
            skLineSegment(sketch, "E662.trimOffspring", {"start": v(-596.72, 230.28) * mm, "end": v(-579.91, 216.2) * mm});
            skPoint(sketch, "E663", {"position": v(-42.76, 249.34) * mm});
            skPoint(sketch, "E664", {"position": v(-199.64, 249.34) * mm});
            skLineSegment(sketch, "E665.0", {"start": v(-64.43, 249.34) * mm, "end": v(49.87, 363.64) * mm});
            skLineSegment(sketch, "E666", {"start": v(93.2, 363.64) * mm, "end": v(93.2, 382.69) * mm});
            skLineSegment(sketch, "E667", {"start": v(49.87, 363.64) * mm, "end": v(49.87, 382.69) * mm});
            skLineSegment(sketch, "E668", {"start": v(49.87, 382.69) * mm, "end": v(93.2, 382.69) * mm});
            skLineSegment(sketch, "E669", {"start": v(-64.43, 249.34) * mm, "end": v(-59.58, 249.34) * mm});
            skLineSegment(sketch, "E670", {"start": v(-25.94, 249.34) * mm, "end": v(-21.1, 249.34) * mm});
            skLineSegment(sketch, "E671.trimOffspring", {"start": v(-21.1, 249.34) * mm, "end": v(93.2, 363.64) * mm});
            skLineSegment(sketch, "E672", {"start": v(-42.76, 249.34) * mm, "end": v(-42.76, 230.28) * mm});
            skLineSegment(sketch, "E673.trimOffspring", {"start": v(-59.58, 249.34) * mm, "end": v(-181, 249.34) * mm, "construction": true});
            skLineSegment(sketch, "E674.0", {"start": v(-221.06, 249.34) * mm, "end": v(-335.36, 363.64) * mm});
            skLineSegment(sketch, "E675.0", {"start": v(-176.16, 249.34) * mm, "end": v(-290.46, 363.64) * mm});
            skLineSegment(sketch, "E676", {"start": v(-176.16, 249.34) * mm, "end": v(-181, 249.34) * mm});
            skLineSegment(sketch, "E677", {"start": v(-218.27, 249.34) * mm, "end": v(-221.06, 249.34) * mm});
            skLineSegment(sketch, "E678", {"start": v(-335.36, 363.64) * mm, "end": v(-335.36, 382.69) * mm});
            skLineSegment(sketch, "E679", {"start": v(-290.46, 363.64) * mm, "end": v(-290.46, 382.69) * mm});
            skLineSegment(sketch, "E680", {"start": v(-290.46, 382.69) * mm, "end": v(-335.36, 382.69) * mm});
            skLineSegment(sketch, "E681", {"start": v(-158.05, -150.07) * mm, "end": v(-158.05, -182.74) * mm, "construction": true});
            skLineSegment(sketch, "E682", {"start": v(-199.64, 249.34) * mm, "end": v(-199.64, 230.29) * mm});
            skPoint(sketch, "E683.orphan", {"position": v(-83.56, -34.55) * mm});
            skLineSegment(sketch, "E684", {"start": v(-85.13, -182.74) * mm, "end": v(-131.12, -182.74) * mm, "construction": true});
            skLineSegment(sketch, "E685", {"start": v(-85.13, -34.56) * mm, "end": v(-158.05, -34.56) * mm});
            skLineSegment(sketch, "E686", {"start": v(-85.13, -150.07) * mm, "end": v(-131.12, -150.07) * mm});
            skLineSegment(sketch, "E687", {"start": v(-85.13, -182.74) * mm, "end": v(-131.12, -182.74) * mm});
            skLineSegment(sketch, "E688", {"start": v(-157.02, -0.16) * mm, "end": v(-143.69, -0.16) * mm});
            skLineSegment(sketch, "E689", {"start": v(-83.56, -0.16) * mm, "end": v(-90.44, -0.16) * mm});
            skPoint(sketch, "E690", {"position": v(-151.32, -17.37) * mm});
            skLineSegment(sketch, "E691", {"start": v(-83.56, -0.16) * mm, "end": v(-96.9, -0.16) * mm});
            skLineSegment(sketch, "E692", {"start": v(-96.9, -0.16) * mm, "end": v(-115.95, 0) * mm});
            skLineSegment(sketch, "E693", {"start": v(-143.69, -0.16) * mm, "end": v(-126.36, -0.01) * mm});
            skPoint(sketch, "E694", {"position": v(-121.6, -34.56) * mm});
            skLineSegment(sketch, "E695", {"start": v(-126.36, -24.23) * mm, "end": v(-116.83, -24.23) * mm});
            skPoint(sketch, "E696", {"position": v(-120.88, -24.93) * mm});
            skLineSegment(sketch, "E697", {"start": v(-121.6, -24.23) * mm, "end": v(-121.6, -23.58) * mm});
            skLineSegment(sketch, "E698", {"start": v(-116.83, -24.23) * mm, "end": v(-116.83, -17.36) * mm});
            skPoint(sketch, "E699.orphan", {"position": v(-116.83, -23.64) * mm});
            skLineSegment(sketch, "E700", {"start": v(-116.83, -17.36) * mm, "end": v(-116.83, 0) * mm});
            skLineSegment(sketch, "E701", {"start": v(-116.83, 0) * mm, "end": v(-115.95, 0) * mm});
            skLineSegment(sketch, "E702", {"start": v(-126.36, -24.23) * mm, "end": v(-126.36, 0) * mm});
            skLineSegment(sketch, "E703", {"start": v(-124.64, -17.36) * mm, "end": v(-126.36, -17.36) * mm});
            skPoint(sketch, "E704.start.orphan", {"position": v(-124.64, 0) * mm});
            skSolve(sketch);
        }
        {
            var Q0;
            Q0=makeQuery(id+"F4.imprint","IMPRINT",FACE,{"disambiguationData":[TD([[makeQuery(id+"F4.imprint","IMPRINT",EDGE,{"derivedFrom":sQuery(id+"F4.wireOp",EDGE,"E214.top")}),-1.0]])]});
            extrude(context, id + "F6", {"entities" : qUnion([Q0]), "endBound" : BoundingType.SYMMETRIC, "depth" : 19.05 * mm});
        }
        {
            var Q0;
            Q0=makeQuery(id+"F5.imprint","IMPRINT",FACE,{"disambiguationData":[TD([[makeQuery(id+"F5.imprint","IMPRINT",EDGE,{"derivedFrom":sQuery(id+"F5.wireOp",EDGE,"E458.top")}),-1.0]])]});
            extrude(context, id + "F7", {"entities" : qUnion([Q0]), "endBound" : BoundingType.SYMMETRIC, "depth" : 19.05 * mm});
        }
        {
            var Q0;
            Q0=qCreatedBy(id+"F1.planeOp",FACE);
            var sketch = newSketch(context, id + "F8", { "sketchPlane" : qUnion([Q0])});
            skLineSegment(sketch, "E705.0", {"start": v(-640.74, 15.45) * mm, "end": v(234.28, 377.87) * mm});
            skLineSegment(sketch, "E706.0", {"start": v(403.6, 9.57) * mm, "end": v(256.36, 364.65) * mm});
            skLineSegment(sketch, "E707.0", {"start": v(-476.6, -376.67) * mm, "end": v(397.36, -15.42) * mm});
            skLineSegment(sketch, "E708.0", {"start": v(-646.9, -9.54) * mm, "end": v(-498.75, -363.46) * mm});
            skPoint(sketch, "E709", {"position": v(256.36, 364.65) * mm});
            skPoint(sketch, "E710", {"position": v(403.6, 9.57) * mm});
            skPoint(sketch, "E711", {"position": v(-498.75, -363.46) * mm});
            skPoint(sketch, "E712", {"position": v(-646.9, -9.54) * mm});
            skLineSegment(sketch, "E713", {"start": v(223.5, 358.78) * mm, "end": v(236.98, 345.25) * mm});
            skLineSegment(sketch, "E714", {"start": v(236.98, 345.25) * mm, "end": v(256.36, 364.65) * mm});
            skLineSegment(sketch, "E715", {"start": v(223.5, 358.78) * mm, "end": v(241.57, 376.86) * mm});
            skLineSegment(sketch, "E716", {"start": v(376.22, 9.54) * mm, "end": v(376.22, -9.56) * mm});
            skLineSegment(sketch, "E717", {"start": v(376.22, -9.56) * mm, "end": v(401.81, -9.57) * mm});
            skLineSegment(sketch, "E718", {"start": v(376.22, 9.54) * mm, "end": v(403.6, 9.57) * mm});
            skLineSegment(sketch, "E719", {"start": v(-619.44, 9.53) * mm, "end": v(-645.19, 9.57) * mm});
            skLineSegment(sketch, "E720", {"start": v(-646.9, -9.54) * mm, "end": v(-619.44, -9.54) * mm});
            skLineSegment(sketch, "E721", {"start": v(-619.44, -9.54) * mm, "end": v(-619.44, 9.53) * mm});
            skLineSegment(sketch, "E722", {"start": v(-498.75, -363.46) * mm, "end": v(-480.6, -345.3) * mm});
            skLineSegment(sketch, "E723", {"start": v(-480.6, -345.3) * mm, "end": v(-467.1, -358.79) * mm});
            skLineSegment(sketch, "E724", {"start": v(-467.1, -358.79) * mm, "end": v(-483.91, -375.65) * mm});
            skLineSegment(sketch, "E725", {"start": v(-182.7, -74.37) * mm, "end": v(-157.72, -49.46) * mm});
            skLineSegment(sketch, "E726", {"start": v(-157.72, -49.46) * mm, "end": v(-171.3, -35.85) * mm});
            skLineSegment(sketch, "E727", {"start": v(-171.3, -35.85) * mm, "end": v(-196.28, -60.76) * mm});
            skLineSegment(sketch, "E728", {"start": v(-182.7, -74.37) * mm, "end": v(-196.28, -60.76) * mm});
            skLineSegment(sketch, "E729", {"start": v(-218.3, -9.52) * mm, "end": v(-181.02, -9.52) * mm});
            skLineSegment(sketch, "E730", {"start": v(-181.02, -9.52) * mm, "end": v(-181.02, 9.55) * mm});
            skLineSegment(sketch, "E731", {"start": v(-181.02, 9.55) * mm, "end": v(-218.3, 9.55) * mm});
            skLineSegment(sketch, "E732", {"start": v(-218.3, -9.52) * mm, "end": v(-218.3, 9.55) * mm});
            skLineSegment(sketch, "E733", {"start": v(-72.33, 36.01) * mm, "end": v(-47.43, 60.9) * mm});
            skLineSegment(sketch, "E734", {"start": v(-47.43, 60.9) * mm, "end": v(-60.9, 74.38) * mm});
            skLineSegment(sketch, "E735", {"start": v(-60.9, 74.38) * mm, "end": v(-85.8, 49.48) * mm});
            skLineSegment(sketch, "E736", {"start": v(-72.33, 36.01) * mm, "end": v(-85.8, 49.48) * mm});
            skLineSegment(sketch, "E737", {"start": v(-59.6, -9.5) * mm, "end": v(-25.92, -9.5) * mm});
            skLineSegment(sketch, "E738", {"start": v(-25.92, -9.5) * mm, "end": v(-25.92, 9.56) * mm});
            skLineSegment(sketch, "E739", {"start": v(-25.92, 9.56) * mm, "end": v(-59.6, 9.56) * mm});
            skLineSegment(sketch, "E740", {"start": v(-59.6, -9.5) * mm, "end": v(-59.6, 9.56) * mm});
            skLineSegment(sketch, "E741", {"start": v(-481.46, -376.66) * mm, "end": v(-483.91, -375.65) * mm});
            skArc(sketch, "E742.filletArc", {"start": v(-481.46, -376.66) * mm, "mid": v(-479.03, -377.15) * mm, "end": v(-476.6, -376.67) * mm});
            skLineSegment(sketch, "E743", {"start": v(400.8, -12) * mm, "end": v(401.81, -9.57) * mm});
            skLineSegment(sketch, "E744", {"start": v(-644.17, 12.01) * mm, "end": v(-645.19, 9.57) * mm});
            skLineSegment(sketch, "E745", {"start": v(239.14, 377.87) * mm, "end": v(241.57, 376.86) * mm});
            skPoint(sketch, "E746.visualSharp", {"position": v(236.71, 378.88) * mm});
            skArc(sketch, "E746.filletArc", {"start": v(239.14, 377.87) * mm, "mid": v(236.71, 378.35) * mm, "end": v(234.28, 377.87) * mm});
            skPoint(sketch, "E747.visualSharp", {"position": v(-643.17, 14.44) * mm});
            skArc(sketch, "E747.filletArc", {"start": v(-640.74, 15.45) * mm, "mid": v(-642.8, 14.07) * mm, "end": v(-644.17, 12.01) * mm});
            skPoint(sketch, "E748.visualSharp", {"position": v(399.8, -14.42) * mm});
            skArc(sketch, "E748.filletArc", {"start": v(397.36, -15.42) * mm, "mid": v(399.43, -14.05) * mm, "end": v(400.8, -12) * mm});
            skSolve(sketch);
        }
        {
            var Q0;
            Q0=makeQuery(id+"F8.imprint","IMPRINT",FACE,{"disambiguationData":[TD([[makeQuery(id+"F8.imprint","IMPRINT",EDGE,{"derivedFrom":sQuery(id+"F8.wireOp",EDGE,"E705.0")}),-1.0]])]});
            extrude(context, id + "F9", {"entities" : qUnion([Q0]), "depth" : 19.05 * mm});
        }
        {
            var Q0;
            Q0=makeQuery(id+"F5.imprint","IMPRINT",FACE,{"disambiguationData":[TD([[makeQuery(id+"F5.imprint","IMPRINT",EDGE,{"derivedFrom":sQuery(id+"F5.wireOp",EDGE,"E491")}),1.0]])]});
            var Q1;
            Q1=makeQuery(id+"F5.imprint","IMPRINT",FACE,{"disambiguationData":[TD([[makeQuery(id+"F5.imprint","IMPRINT",EDGE,{"derivedFrom":sQuery(id+"F5.wireOp",EDGE,"E564.MirrorCS")}),-1.0]])]});
            extrude(context, id + "F10", {"entities" : qUnion([Q0, Q1]), "endBound" : BoundingType.SYMMETRIC, "depth" : 19.05 * mm});
        }
        {
            var Q0;
            Q0=makeQuery(id+"F4.imprint","IMPRINT",FACE,{"disambiguationData":[TD([[makeQuery(id+"F4.imprint","IMPRINT",EDGE,{"derivedFrom":sQuery(id+"F4.wireOp",EDGE,"E320.MirrorCS")}),-1.0]])]});
            var Q1;
            Q1=makeQuery(id+"F4.imprint","IMPRINT",FACE,{"disambiguationData":[TD([[makeQuery(id+"F4.imprint","IMPRINT",EDGE,{"derivedFrom":sQuery(id+"F4.wireOp",EDGE,"E247")}),1.0]])]});
            extrude(context, id + "F11", {"entities" : qUnion([Q0, Q1]), "endBound" : BoundingType.SYMMETRIC, "depth" : 19.05 * mm});
        }
        {
            var Q0;
            Q0=qCreatedBy(id+"F2.planeOp",FACE);
            var sketch = newSketch(context, id + "F12", { "sketchPlane" : qUnion([Q0])});
            skLineSegment(sketch, "E749", {"start": v(494.04, -9.5) * mm, "end": v(462.24, -9.5) * mm});
            skLineSegment(sketch, "E750", {"start": v(462.24, -9.5) * mm, "end": v(462.24, 9.57) * mm});
            skLineSegment(sketch, "E751", {"start": v(462.24, 9.57) * mm, "end": v(493.99, 9.53) * mm});
            skLineSegment(sketch, "E752", {"start": v(306.76, 442.05) * mm, "end": v(284.27, 419.52) * mm});
            skLineSegment(sketch, "E753", {"start": v(284.27, 419.52) * mm, "end": v(297.77, 406.05) * mm});
            skLineSegment(sketch, "E754", {"start": v(297.77, 406.05) * mm, "end": v(320.23, 428.54) * mm});
            skLineSegment(sketch, "E755", {"start": v(-737.16, 9.56) * mm, "end": v(-705.4, 9.56) * mm});
            skLineSegment(sketch, "E756", {"start": v(-705.4, 9.56) * mm, "end": v(-705.4, -9.52) * mm});
            skLineSegment(sketch, "E757", {"start": v(-705.4, -9.52) * mm, "end": v(-737.2, -9.51) * mm});
            skLineSegment(sketch, "E758", {"start": v(-550.34, -442.02) * mm, "end": v(-527.9, -419.56) * mm});
            skLineSegment(sketch, "E759", {"start": v(-527.9, -419.56) * mm, "end": v(-541.35, -406.1) * mm});
            skLineSegment(sketch, "E760", {"start": v(-541.35, -406.1) * mm, "end": v(-563.78, -428.55) * mm});
            skPoint(sketch, "E761", {"position": v(-28.15, -225.76) * mm});
            skLineSegment(sketch, "E762", {"start": v(-57.32, -155.37) * mm, "end": v(-215.23, 225.8) * mm, "construction": true});
            skPoint(sketch, "E763", {"position": v(-650.5, -219.03) * mm});
            skLineSegment(sketch, "E764", {"start": v(-57.32, -155.37) * mm, "end": v(153.88, -67.87) * mm});
            skLineSegment(sketch, "E765", {"start": v(153.88, -67.87) * mm, "end": v(-57.32, -155.37) * mm});
            skLineSegment(sketch, "E766", {"start": v(-57.32, -155.37) * mm, "end": v(-268.5, -242.86) * mm});
            skLineSegment(sketch, "E767", {"start": v(153.88, -67.87) * mm, "end": v(316.77, -89.3) * mm});
            skLineSegment(sketch, "E768", {"start": v(-650.5, -219.03) * mm, "end": v(407.25, 218.7) * mm, "construction": true});
            skLineSegment(sketch, "E769", {"start": v(-268.5, -242.86) * mm, "end": v(-368.37, -373.02) * mm});
            skLineSegment(sketch, "E770", {"start": v(129.5, 113.01) * mm, "end": v(129.5, 100.25) * mm});
            skLineSegment(sketch, "E771", {"start": v(255.5, 142.67) * mm, "end": v(266.51, 170.86) * mm});
            skLineSegment(sketch, "E772", {"start": v(266.51, 170.86) * mm, "end": v(129.5, 113.01) * mm});
            skLineSegment(sketch, "E773", {"start": v(191.26, 194.48) * mm, "end": v(263.24, 177.4) * mm});
            skLineSegment(sketch, "E774", {"start": v(191.26, 194.48) * mm, "end": v(170.98, 184.84) * mm});
            skLineSegment(sketch, "E775", {"start": v(170.98, 184.84) * mm, "end": v(152.05, 164.14) * mm});
            skLineSegment(sketch, "E776", {"start": v(152.05, 164.14) * mm, "end": v(129.8, 122.2) * mm});
            skLineSegment(sketch, "E777", {"start": v(254.12, 135.67) * mm, "end": v(217.08, 94.02) * mm});
            skLineSegment(sketch, "E778", {"start": v(217.08, 94.02) * mm, "end": v(132.75, 93.96) * mm});
            skLineSegment(sketch, "E779", {"start": v(183.9, 308.48) * mm, "end": v(167.52, 296.1) * mm});
            skLineSegment(sketch, "E780", {"start": v(167.52, 296.1) * mm, "end": v(184.57, 285.27) * mm});
            skLineSegment(sketch, "E781", {"start": v(184.57, 285.27) * mm, "end": v(183.9, 308.48) * mm});
            skLineSegment(sketch, "E782", {"start": v(162, 290.68) * mm, "end": v(182.88, 277.32) * mm});
            skPoint(sketch, "E782.startSnap0", {"position": v(176.04, 290.68) * mm});
            skLineSegment(sketch, "E783", {"start": v(182.88, 277.32) * mm, "end": v(194.08, 251.87) * mm});
            skLineSegment(sketch, "E784", {"start": v(194.08, 251.87) * mm, "end": v(164.58, 243.15) * mm});
            skLineSegment(sketch, "E785", {"start": v(164.58, 243.15) * mm, "end": v(146.47, 245.9) * mm});
            skLineSegment(sketch, "E786", {"start": v(146.47, 245.9) * mm, "end": v(143.5, 269.25) * mm});
            skLineSegment(sketch, "E787", {"start": v(143.5, 269.25) * mm, "end": v(162, 290.68) * mm});
            skLineSegment(sketch, "E788", {"start": v(191.36, 310.52) * mm, "end": v(191.36, 281.37) * mm});
            skLineSegment(sketch, "E789", {"start": v(191.36, 281.37) * mm, "end": v(202.65, 253.2) * mm});
            skLineSegment(sketch, "E790", {"start": v(202.65, 253.2) * mm, "end": v(213.6, 257.59) * mm});
            skLineSegment(sketch, "E791", {"start": v(213.6, 257.59) * mm, "end": v(191.36, 310.52) * mm});
            skLineSegment(sketch, "E792.MirrorCS", {"start": v(-530.06, -50.35) * mm, "end": v(-540.9, -55) * mm});
            skLineSegment(sketch, "E793.MirrorCS", {"start": v(-535.55, 4.81) * mm, "end": v(-539.95, -14.89) * mm});
            skLineSegment(sketch, "E794.MirrorCS", {"start": v(-555.9, 2) * mm, "end": v(-535.55, 4.81) * mm});
            skLineSegment(sketch, "E795.MirrorCS", {"start": v(-496.04, -30.53) * mm, "end": v(-485.18, -15.78) * mm});
            skLineSegment(sketch, "E796.MirrorCS", {"start": v(-527.83, 4.9) * mm, "end": v(-533.14, -19.32) * mm});
            skLineSegment(sketch, "E797.MirrorCS", {"start": v(-539.95, -14.89) * mm, "end": v(-555.9, 2) * mm});
            skPoint(sketch, "E798.MirrorP", {"position": v(-537.75, -5.04) * mm});
            skLineSegment(sketch, "E799.MirrorCS", {"start": v(-499.59, 2.83) * mm, "end": v(-527.83, 4.9) * mm});
            skLineSegment(sketch, "E800.MirrorCS", {"start": v(-542, -22.45) * mm, "end": v(-530.06, -50.35) * mm});
            skLineSegment(sketch, "E801.MirrorCS", {"start": v(-533.14, -19.32) * mm, "end": v(-523.06, -45.23) * mm});
            skLineSegment(sketch, "E802.MirrorCS", {"start": v(-562.6, -1.85) * mm, "end": v(-542, -22.45) * mm});
            skLineSegment(sketch, "E803.MirrorCS", {"start": v(-485.18, -15.78) * mm, "end": v(-499.59, 2.83) * mm});
            skLineSegment(sketch, "E804.MirrorCS", {"start": v(-523.06, -45.23) * mm, "end": v(-496.04, -30.53) * mm});
            skLineSegment(sketch, "E805.MirrorCS", {"start": v(-540.9, -55) * mm, "end": v(-562.6, -1.85) * mm});
            skLineSegment(sketch, "E806", {"start": v(494.04, -9.5) * mm, "end": v(494.03, -11.68) * mm});
            skLineSegment(sketch, "E807", {"start": v(493.99, 9.53) * mm, "end": v(494, 14.61) * mm});
            skLineSegment(sketch, "E808", {"start": v(306.76, 442.05) * mm, "end": v(305.27, 443.54) * mm});
            skLineSegment(sketch, "E809", {"start": v(320.23, 428.54) * mm, "end": v(323.83, 424.95) * mm});
            skLineSegment(sketch, "E810", {"start": v(-737.16, 9.56) * mm, "end": v(-737.17, 11.65) * mm});
            skLineSegment(sketch, "E811", {"start": v(-737.2, -9.51) * mm, "end": v(-737.2, -14.6) * mm});
            skLineSegment(sketch, "E812", {"start": v(-563.78, -428.55) * mm, "end": v(-567.38, -424.96) * mm});
            skLineSegment(sketch, "E813", {"start": v(-550.34, -442.02) * mm, "end": v(-548.82, -443.53) * mm});
            skLineSegment(sketch, "E814", {"start": v(-568.76, -422.9) * mm, "end": v(-736.72, -17.03) * mm});
            skLineSegment(sketch, "E815", {"start": v(-733.25, 17.54) * mm, "end": v(298.35, 444.91) * mm});
            skLineSegment(sketch, "E816", {"start": v(325.21, 422.89) * mm, "end": v(493.5, 17.05) * mm});
            skLineSegment(sketch, "E817", {"start": v(-541.92, -444.89) * mm, "end": v(-368.37, -373.02) * mm});
            skLineSegment(sketch, "E818.trimOffspring", {"start": v(316.77, -89.3) * mm, "end": v(490.11, -17.53) * mm});
            skPoint(sketch, "E819.visualSharp", {"position": v(494.02, -15.91) * mm});
            skArc(sketch, "E819.filletArc", {"start": v(490.11, -17.53) * mm, "mid": v(492.96, -15.2) * mm, "end": v(494.03, -11.68) * mm});
            skPoint(sketch, "E820.visualSharp", {"position": v(494, 15.88) * mm});
            skArc(sketch, "E820.filletArc", {"start": v(494, 14.61) * mm, "mid": v(493.87, 15.85) * mm, "end": v(493.5, 17.05) * mm});
            skPoint(sketch, "E821.visualSharp", {"position": v(-545.82, -446.5) * mm});
            skArc(sketch, "E821.filletArc", {"start": v(-548.82, -443.53) * mm, "mid": v(-545.58, -445.25) * mm, "end": v(-541.92, -444.89) * mm});
            skPoint(sketch, "E822.visualSharp", {"position": v(-568.28, -424.06) * mm});
            skArc(sketch, "E822.filletArc", {"start": v(-568.76, -422.9) * mm, "mid": v(-568.17, -424) * mm, "end": v(-567.38, -424.96) * mm});
            skPoint(sketch, "E823.visualSharp", {"position": v(324.73, 424.06) * mm});
            skArc(sketch, "E823.filletArc", {"start": v(325.21, 422.89) * mm, "mid": v(324.62, 423.99) * mm, "end": v(323.83, 424.95) * mm});
            skPoint(sketch, "E824.visualSharp", {"position": v(302.27, 446.54) * mm});
            skArc(sketch, "E824.filletArc", {"start": v(305.27, 443.54) * mm, "mid": v(302.02, 445.27) * mm, "end": v(298.35, 444.91) * mm});
            skPoint(sketch, "E825.visualSharp", {"position": v(-737.18, 15.91) * mm});
            skArc(sketch, "E825.filletArc", {"start": v(-733.25, 17.54) * mm, "mid": v(-736.1, 15.2) * mm, "end": v(-737.17, 11.65) * mm});
            skPoint(sketch, "E826.visualSharp", {"position": v(-737.2, -15.86) * mm});
            skArc(sketch, "E826.filletArc", {"start": v(-737.2, -14.6) * mm, "mid": v(-737.08, -15.84) * mm, "end": v(-736.72, -17.03) * mm});
            skSolve(sketch);
        }
        {
            var Q0;
            Q0=makeQuery(id+"F12.imprint","IMPRINT",FACE,{"disambiguationData":[TD([[makeQuery(id+"F12.imprint","IMPRINT",EDGE,{"derivedFrom":sQuery(id+"F12.wireOp",EDGE,"E749")}),1.0]])]});
            extrude(context, id + "F13", {"entities" : qUnion([Q0]), "depth" : 19.05 * mm});
        }
    });
